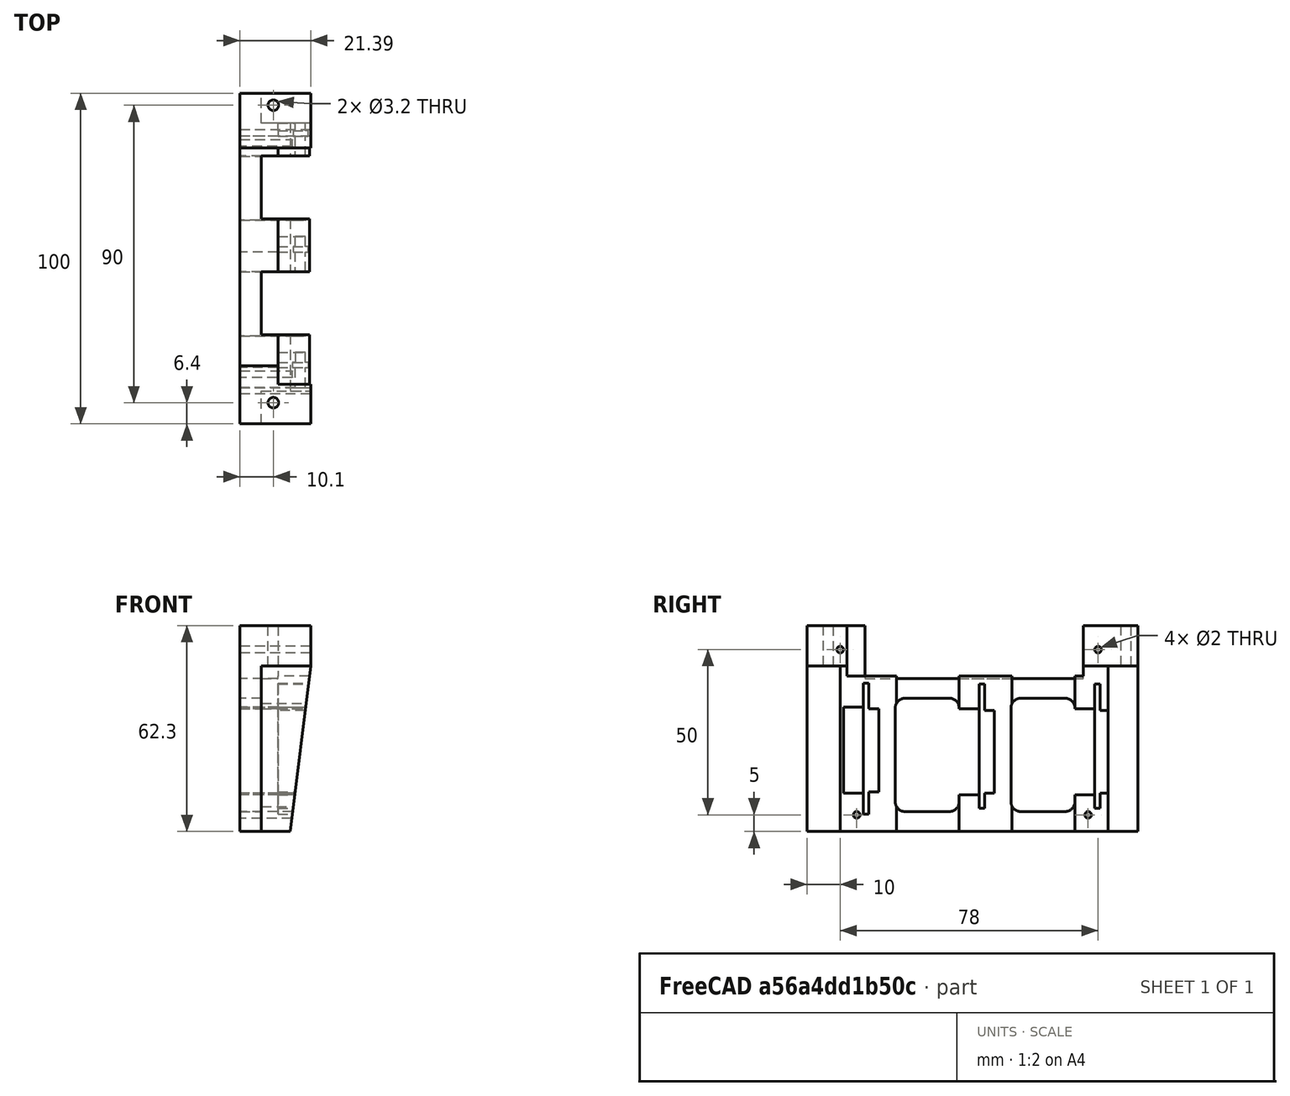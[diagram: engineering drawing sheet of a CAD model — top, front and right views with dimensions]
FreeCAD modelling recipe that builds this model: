
FCSTD DOCUMENT  (FreeCAD 1.1R40938 (Git))
Label: sborka
License: All rights reserved
LicenseURL: https://en.wikipedia.org/wiki/All_rights_reserved
objects: App::Link×10, Sketcher::SketchObject×6, PartDesign::Pocket×5, PartDesign::Pad×2, App::Point×2, Assembly::JointGroup×1, PartDesign::Body×1, Assembly::AssemblyObject×1
note: 34 computed .brp shape members not serialized (recipe doc carries the construction recipe); baked Part::Feature solids carry a one-line shape summary decoded from their .brp
EXTERNAL_REF file=lcd.FCStd obj=__97inch_LCD
EXTERNAL_REF file=ADC.FCStd obj=Board_3770
EXTERNAL_REF file=KEYPAD.FCStd obj=Body
EXTERNAL_REF file=fpga.FCStd obj=Board_4879
EXTERNAL_REF file=dac.FCStd obj=Board_2375
EXTERNAL_REF file=fpga_ext_board.FCStd obj=Board_e45
EXTERNAL_REF file=acd_dac_board.FCStd obj=Board_c5fe
EXTERNAL_REF file=power_supply.FCStd obj=Board_7c43
EXTERNAL_REF file=frontpanel.FCStd obj=Body

FEATURE [Assembly::JointGroup] Joints
FEATURE [App::Link] __97inch_LCD001  label="3_97inch_LCD001"
  LinkPlacement = pos=(582.68,421.04,26.49) rot=(0,0,-1;1.5708rad)
  LinkedObject = -> <external lcd.FCStd>#__97inch_LCD
  Placement = pos=(582.68,421.04,26.49) rot=(0,0,-1;1.5708rad)
FEATURE [App::Link] adc
  LinkPlacement = pos=(484.6,367,13) rot=(0.57735,0.57735,-0.57735;2.0944rad)
  LinkedObject = -> <external ADC.FCStd>#Board_3770
  Placement = pos=(484.6,367,13) rot=(0.57735,0.57735,-0.57735;2.0944rad)
FEATURE [App::Link] adc001
  LinkPlacement = pos=(484.6,332,13) rot=(0.57735,0.57735,-0.57735;2.0944rad)
  LinkedObject = -> <external ADC.FCStd>#Board_3770
  Placement = pos=(484.6,332,13) rot=(0.57735,0.57735,-0.57735;2.0944rad)
FEATURE [App::Link] Body  label="keypad"
  LinkPlacement = pos=(611.73,395.16,29.88) rot=(-1,0,0;1.5708rad)
  LinkedObject = -> <external KEYPAD.FCStd>#Body
  Placement = pos=(611.73,395.16,29.88) rot=(-1,0,0;1.5708rad)
FEATURE [App::Link] fpga
  LinkPlacement = pos=(542.88,295.2,49.34) rot=(0.707107,0.707107,0;3.14159rad)
  LinkedObject = -> <external fpga.FCStd>#Board_4879
  Placement = pos=(542.88,295.2,49.34) rot=(0.707107,0.707107,0;3.14159rad)
FEATURE [App::Link] dac
  LinkPlacement = pos=(481.74,297,5.5) rot=(-0.57735,-0.57735,0.57735;4.18879rad)
  LinkedObject = -> <external dac.FCStd>#Board_2375
  Placement = pos=(481.74,297,5.5) rot=(-0.57735,-0.57735,0.57735;4.18879rad)
FEATURE [App::Link] fpga_ext_board
  LinkPlacement = pos=(419,436.7,62.5) rot=(-0.707107,0.707107,0;3.14159rad)
  LinkedObject = -> <external fpga_ext_board.FCStd>#Board_e45
  Placement = pos=(419,436.7,62.5) rot=(-0.707107,0.707107,0;3.14159rad)
FEATURE [App::Link] acd_dac_board
  LinkPlacement = pos=(472,468,-70) rot=(-0.57735,0.57735,-0.57735;2.0944rad)
  LinkedObject = -> <external acd_dac_board.FCStd>#Board_c5fe
  Placement = pos=(472,468,-70) rot=(-0.57735,0.57735,-0.57735;2.0944rad)
FEATURE [Sketcher::SketchObject] Sketch
  ArcFitTolerance = 1e-06
  AttachmentSupport = -> [YZ_Plane001]
  ExternalTypes = [0]
  FullyConstrained = true
  MakeInternals = false
  MapMode = 5
  Placement = pos=(0,0,0) rot=(0.57735,0.57735,0.57735;2.0944rad)
  sketch-geometry (69):
    g0: LineSegment StartX=-33 StartY=5.25 StartZ=0 EndX=-31.36 EndY=5.25 EndZ=0
    g1: LineSegment StartX=-31.36 StartY=5.25 StartZ=0 EndX=-31.36 EndY=11.95 EndZ=0
    g2: LineSegment StartX=-31.36 StartY=44.85 StartZ=0 EndX=-33 EndY=44.85 EndZ=0
    g3: LineSegment StartX=2 StartY=7 StartZ=0 EndX=3.64 EndY=7 EndZ=0
    g4: LineSegment StartX=3.64 StartY=7 StartZ=0 EndX=3.64 EndY=11.6 EndZ=0
    g5: LineSegment StartX=3.64 StartY=44.6 StartZ=0 EndX=2 EndY=44.6 EndZ=0
    g6: LineSegment StartX=37 StartY=7 StartZ=0 EndX=38.64 EndY=7 EndZ=0
    g7: LineSegment StartX=38.64 StartY=7 StartZ=0 EndX=38.64 EndY=11.6 EndZ=0
    g8: LineSegment StartX=38.64 StartY=44.6 StartZ=0 EndX=37 EndY=44.6 EndZ=0
    g9: LineSegment StartX=-50 StartY=62.3 StartZ=0 EndX=-50 EndY=0 EndZ=0
    g10: LineSegment StartX=-50 StartY=0 StartZ=0 EndX=50 EndY=0 EndZ=0
    g11: LineSegment StartX=50 StartY=0 StartZ=0 EndX=50 EndY=62.3 EndZ=0
    g12: LineSegment StartX=-32.5 StartY=46.3 StartZ=0 EndX=33.5 EndY=46.3 EndZ=0
    g13: LineSegment StartX=-31.36 StartY=11.95 StartZ=0 EndX=-28.36 EndY=11.95 EndZ=0
    g14: LineSegment StartX=-28.36 StartY=11.95 StartZ=0 EndX=-28.36 EndY=37.15 EndZ=0
    g15: LineSegment StartX=-28.36 StartY=37.15 StartZ=0 EndX=-31.36 EndY=37.15 EndZ=0
    g16: LineSegment StartX=3.64 StartY=11.6 StartZ=0 EndX=6.64 EndY=11.6 EndZ=0
    g17: LineSegment StartX=6.64 StartY=11.6 StartZ=0 EndX=6.64 EndY=36.6 EndZ=0
    g18: LineSegment StartX=6.64 StartY=36.6 StartZ=0 EndX=3.64 EndY=36.6 EndZ=0
    g19: LineSegment StartX=38.64 StartY=11.6 StartZ=0 EndX=41.64 EndY=11.6 EndZ=0
    g20: LineSegment StartX=41.64 StartY=11.6 StartZ=0 EndX=41.64 EndY=36.6 EndZ=0
    g21: LineSegment StartX=41.64 StartY=36.6 StartZ=0 EndX=38.64 EndY=36.6 EndZ=0
    g22: LineSegment StartX=-31.36 StartY=37.15 StartZ=0 EndX=-31.36 EndY=44.85 EndZ=0
    g23: LineSegment StartX=3.64 StartY=36.6 StartZ=0 EndX=3.64 EndY=44.6 EndZ=0
    g24: LineSegment StartX=38.64 StartY=36.6 StartZ=0 EndX=38.64 EndY=44.6 EndZ=0
    g25: LineSegment StartX=-32.5 StartY=52.3 StartZ=0 EndX=33.5 EndY=52.3 EndZ=0
    g26: LineSegment StartX=-32.5 StartY=62.3 StartZ=0 EndX=-50 EndY=62.3 EndZ=0
    g27: LineSegment StartX=-32.5 StartY=62.3 StartZ=0 EndX=-32.5 EndY=52.3 EndZ=0
    g28: LineSegment StartX=-32.5 StartY=52.3 StartZ=0 EndX=-32.5 EndY=46.3 EndZ=0
    g29: LineSegment StartX=33.5 StartY=46.3 StartZ=0 EndX=33.5 EndY=52.3 EndZ=0
    g30: LineSegment StartX=33.5 StartY=52.3 StartZ=0 EndX=33.5 EndY=62.3 EndZ=0
    g31: LineSegment StartX=50 StartY=62.3 StartZ=0 EndX=33.5 EndY=62.3 EndZ=0
    g32: LineSegment StartX=-23.36 StartY=37.3 StartZ=0 EndX=-23.36 EndY=9 EndZ=0
    g33: LineSegment StartX=-20.36 StartY=6 StartZ=0 EndX=-7 EndY=6 EndZ=0
    g34: LineSegment StartX=-4 StartY=9 StartZ=0 EndX=-4 EndY=11.1 EndZ=0
    g35: LineSegment StartX=-7 StartY=40.3 StartZ=0 EndX=-20.36 EndY=40.3 EndZ=0
    g36: ArcOfCircle CenterX=-20.36 CenterY=37.3 CenterZ=0 NormalX=0 NormalY=0 NormalZ=1 AngleXU=0 Radius=3 StartAngle=1.5708 EndAngle=3.14159
    g37: ArcOfCircle CenterX=-20.36 CenterY=9 CenterZ=0 NormalX=0 NormalY=0 NormalZ=1 AngleXU=0 Radius=3 StartAngle=3.14159 EndAngle=4.71239
    g38: ArcOfCircle CenterX=-7 CenterY=9 CenterZ=0 NormalX=0 NormalY=0 NormalZ=1 AngleXU=0 Radius=3 StartAngle=4.71239 EndAngle=6.28319
    g39: ArcOfCircle CenterX=-7 CenterY=37.3 CenterZ=0 NormalX=0 NormalY=0 NormalZ=1 AngleXU=0 Radius=3 StartAngle=6.21647 EndAngle=7.85398
    g40: GeomPoint [constr] X=-23.36 Y=40.3 Z=0
    g41: GeomPoint [constr] X=-4 Y=6 Z=0
    g42: LineSegment StartX=11.64 StartY=37.3 StartZ=0 EndX=11.64 EndY=9 EndZ=0
    g43: LineSegment StartX=14.64 StartY=6 StartZ=0 EndX=28 EndY=6 EndZ=0
    g44: LineSegment StartX=31 StartY=9 StartZ=0 EndX=31 EndY=11.1 EndZ=0
    g45: LineSegment StartX=28 StartY=40.3 StartZ=0 EndX=14.64 EndY=40.3 EndZ=0
    g46: ArcOfCircle CenterX=14.64 CenterY=37.3 CenterZ=0 NormalX=0 NormalY=0 NormalZ=1 AngleXU=0 Radius=3 StartAngle=1.5708 EndAngle=3.14159
    g47: ArcOfCircle CenterX=14.64 CenterY=9 CenterZ=0 NormalX=0 NormalY=0 NormalZ=1 AngleXU=0 Radius=3 StartAngle=3.14159 EndAngle=4.71239
    g48: ArcOfCircle CenterX=28 CenterY=9 CenterZ=0 NormalX=0 NormalY=0 NormalZ=1 AngleXU=0 Radius=3 StartAngle=4.71239 EndAngle=6.28319
    g49: ArcOfCircle CenterX=28 CenterY=37.3 CenterZ=0 NormalX=0 NormalY=0 NormalZ=1 AngleXU=0 Radius=3 StartAngle=6.21647 EndAngle=7.85398
    g50: GeomPoint [constr] X=11.64 Y=40.3 Z=0
    g51: GeomPoint [constr] X=31 Y=6 Z=0
    g52: LineSegment StartX=-33 StartY=37.55 StartZ=0 EndX=-39 EndY=37.55 EndZ=0
    g53: LineSegment StartX=-39 StartY=37.55 StartZ=0 EndX=-39 EndY=11.55 EndZ=0
    g54: LineSegment StartX=-39 StartY=11.55 StartZ=0 EndX=-33 EndY=11.55 EndZ=0
    g55: LineSegment StartX=-33 StartY=11.55 StartZ=0 EndX=-33 EndY=37.55 EndZ=0
    g56: LineSegment StartX=-33 StartY=11.55 StartZ=0 EndX=-33 EndY=5.25 EndZ=0
    g57: LineSegment StartX=-33 StartY=44.85 StartZ=0 EndX=-33 EndY=37.55 EndZ=0
    g58: LineSegment StartX=-33 StartY=37.55 StartZ=0 EndX=-33 EndY=11.55 EndZ=0
    g59: LineSegment StartX=2 StartY=37.1 StartZ=0 EndX=-4.00667 EndY=37.1 EndZ=0
    g60: LineSegment StartX=2 StartY=11.1 StartZ=0 EndX=-4 EndY=11.1 EndZ=0
    g61: LineSegment StartX=37 StartY=37.1 StartZ=0 EndX=30.9933 EndY=37.1 EndZ=0
    g62: LineSegment StartX=31 StartY=11.1 StartZ=0 EndX=37 EndY=11.1 EndZ=0
    g63: LineSegment StartX=2 StartY=44.6 StartZ=0 EndX=2 EndY=37.1 EndZ=0
    g64: LineSegment StartX=2 StartY=37.1 StartZ=0 EndX=2 EndY=11.1 EndZ=0
    g65: LineSegment StartX=2 StartY=11.1 StartZ=0 EndX=2 EndY=7 EndZ=0
    g66: LineSegment StartX=37 StartY=11.1 StartZ=0 EndX=37 EndY=7 EndZ=0
    g67: LineSegment StartX=37 StartY=44.6 StartZ=0 EndX=37 EndY=37.1 EndZ=0
    g68: LineSegment StartX=37 StartY=37.1 StartZ=0 EndX=37 EndY=11.1 EndZ=0
  constraints (191):
    c: Coincident(g56,g0)
    c: Coincident(g0,g1)
    c: Coincident(g22,g2)
    c: Coincident(g2,g57)
    c: Vertical(g1)
    c: Horizontal(g0)
    c: Horizontal(g2)
    c: Distance(g57,g22) = 1.64
    c: Distance(g0,g2) = 39.6
    c: Coincident(g65,g3)
    c: Coincident(g3,g4)
    c: Coincident(g23,g5)
    c: Coincident(g5,g63)
    c: Vertical(g4)
    c: Horizontal(g3)
    c: Horizontal(g5)
    c: Distance(g63,g23) = 1.64
    c: Distance(g3,g5) = 37.6
    c: Coincident(g66,g6)
    c: Coincident(g6,g7)
    c: Coincident(g24,g8)
    c: Coincident(g8,g67)
    c: Vertical(g7)
    c: Horizontal(g6)
    c: Horizontal(g8)
    c: Distance(g67,g24) = 1.64
    c: Distance(g6,g8) = 37.6
    c: Horizontal(g23,g67)
    c: DistanceX(g63,g67) = 35
    c: DistanceX(g57,g63) = 35
    c: DistanceY(g63,g22) = 0.25
    c: Distance(g66,g-1) = 7
    c: Coincident(g9,g10)
    c: Coincident(g10,g11)
    c: Coincident(g26,g9)
    c: Vertical(g9)
    c: Vertical(g11)
    c: Horizontal(g10)
    c: PointOnObject(g10,g-1)
    c: Coincident(g28,g12)
    c: Coincident(g12,g29)
    c: Horizontal(g12)
    c: Distance(g27,g30) = 66
    c: Distance(g12,g27) = 16
    c: DistanceY(g9,g9) = 62.3
    c: DistanceX(g10,g10) = 100
    c: Coincident(g13,g14)
    c: Coincident(g14,g15)
    c: Vertical(g14)
    c: Horizontal(g13)
    c: Horizontal(g15)
    c: Distance(g15,g14) = 3
    c: Distance(g13,g15) = 25.2
    c: Distance(g56,g9) = 17
    c: DistanceY(g15,g22) = 7.7
    c: Coincident(g16,g17)
    c: Coincident(g17,g18)
    c: Vertical(g17)
    c: Horizontal(g16)
    c: Horizontal(g18)
    c: Distance(g18,g17) = 3
    c: Distance(g16,g18) = 25
    c: Coincident(g19,g20)
    c: Coincident(g20,g21)
    c: Vertical(g20)
    c: Horizontal(g19)
    c: Horizontal(g21)
    c: Distance(g21,g21) = 3
    c: DistanceY(g20,g20) = 25
    c: DistanceY(g21,g24) = 8
    c: DistanceY(g17,g23) = 8
    c: Symmetric(g9,g11,g-2)
    c: Equal(g21,g19)
    c: Equal(g13,g15)
    c: Equal(g16,g18)
    c: Coincident(g1,g13)
    c: Coincident(g4,g16)
    c: Coincident(g7,g19)
    c: Coincident(g21,g24)
    c: Coincident(g23,g18)
    c: Vertical(g24)
    c: Vertical(g23)
    c: Coincident(g22,g15)
    c: Vertical(g22)
    c: Horizontal(g25)
    c: DistanceY(g12,g25) = 6
    c: Coincident(g27,g28)
    c: Vertical(g27)
    c: Vertical(g28)
    c: Distance(g9,g27) = 17.5
    c: Coincident(g29,g30)
    c: Vertical(g29)
    c: Vertical(g30)
    c: Coincident(g27,g25)
    c: Coincident(g31,g11)
    c: Coincident(g31,g30)
    c: Horizontal(g31)
    c: Horizontal(g26)
    c: Coincident(g26,g27)
    c: Coincident(g29,g25)
    c: Tangent(g32,g36) = -1.5708
    c: Tangent(g32,g37) = -1.5708
    c: Tangent(g33,g37) = -1.5708
    c: Tangent(g33,g38) = -1.5708
    c: Tangent(g34,g38) = -1.5708
    c: Tangent(g35,g39) = -1.5708
    c: Tangent(g35,g36) = -1.5708
    c: Vertical(g32)
    c: Vertical(g34)
    c: Horizontal(g33)
    c: Horizontal(g35)
    c: Equal(g36,g37)
    c: Equal(g37,g38)
    c: Equal(g38,g39)
    c: PointOnObject(g40,g32)
    c: PointOnObject(g40,g35)
    c: PointOnObject(g41,g33)
    c: PointOnObject(g41,g34)
    c: Radius(g37) = 3
    c: Tangent(g42,g46) = -1.5708
    c: Tangent(g42,g47) = -1.5708
    c: Tangent(g43,g47) = -1.5708
    c: Tangent(g43,g48) = -1.5708
    c: Tangent(g44,g48) = -1.5708
    c: Tangent(g45,g49) = -1.5708
    c: Tangent(g45,g46) = -1.5708
    c: Vertical(g42)
    c: Vertical(g44)
    c: Horizontal(g43)
    c: Horizontal(g45)
    c: Equal(g46,g47)
    c: Equal(g47,g48)
    c: Equal(g48,g49)
    c: PointOnObject(g50,g42)
    c: PointOnObject(g50,g45)
    c: PointOnObject(g51,g43)
    c: PointOnObject(g51,g44)
    c: Radius(g47) = 3
    c: Distance(g32,g14) = 5
    c: Distance(g42,g17) = 5
    c: Distance(g35,g12) = 6
    c: Distance(g45,g12) = 6
    c: Distance(g33,g10) = 6
    c: Distance(g43,g10) = 6
    c: Coincident(g52,g53)
    c: Coincident(g53,g54)
    c: Coincident(g54,g55)
    c: Coincident(g55,g52)
    c: Horizontal(g52)
    c: Horizontal(g54)
    c: Vertical(g53)
    c: Vertical(g55)
    c: Distance(g53,g55) = 6
    c: Distance(g52,g54) = 26
    c: DistanceY(g15,g52) = 0.4
    c: Coincident(g58,g56)
    c: Vertical(g56)
    c: Coincident(g58,g54)
    c: Coincident(g57,g58)
    c: Vertical(g57)
    c: Coincident(g57,g52)
    c: Horizontal(g59)
    c: Horizontal(g60)
    c: DistanceY(g60,g4) = 0.5
    c: Coincident(g34,g60)
    c: Coincident(g39,g59)
    c: Vertical(g38,g39)
    c: DistanceX(g60,g60) = 6
    c: Horizontal(g61)
    c: Horizontal(g62)
    c: DistanceY(g62,g7) = 0.5
    c: Coincident(g44,g62)
    c: Coincident(g49,g61)
    c: Vertical(g48,g49)
    c: Distance(g18,g59) = 0.5
    c: Distance(g21,g61) = 0.5
    c: Coincident(g63,g64)
    c: Vertical(g63)
    c: PointOnObject(g60,g63)
    c: Coincident(g63,g59)
    c: Coincident(g64,g65)
    c: Vertical(g65)
    c: Coincident(g64,g60)
    c: Coincident(g68,g66)
    c: Vertical(g66)
    c: Coincident(g68,g62)
    c: Coincident(g67,g68)
    c: Vertical(g67)
    c: Vertical(g68)
    c: Distance(g44,g67) = 6
    c: Coincident(g67,g61)
FEATURE [PartDesign::Pad] Pad
  Direction = (1,0,0)
  Length = 11.5
  Length2 = 10
  Placement = pos=(0,0,0) rot=(1,1,1;2.0944rad)
  Profile = -> Sketch [Edge59,Edge60,Edge61,Edge65,Edge64,Edge63,Edge55,Edge56,Edge57,Edge58,Edge37,Edge53,Edge51,Vertex49,Edge52,Edge50,Edge49,Edge48,Edge47,Edge46,Edge45,Edge44,Edge15,Edge25,Edge26,Edge27,Edge28,Edge29,Edge30,Edge31,Edge32,Vertex30,Vertex31,Edge34,Edge33,Edge11,Edge10,Edge12,Edge9]
  ReferenceAxis = -> Sketch [N_Axis]
  Refine = true
  Reversed = true
  Suppressed = false
  Type = 0
FEATURE [PartDesign::Pad] Pad001
  BaseFeature = -> Pad
  Direction = (1,0,0)
  Length = 10
  Length2 = 10
  Placement = pos=(0,0,0) rot=(1,1,1;2.0944rad)
  Profile = -> Sketch [Edge59,Edge60,Edge61,Vertex60,Edge55,Edge56,Edge57,Vertex38,Edge40,Edge39,Edge41,Edge62,Edge43,Edge42,Edge44,Edge45,Edge46,Edge47,Edge48,Vertex34,Edge38,Edge36,Edge35,Edge54,Edge53,Vertex49,Edge52,Edge51,Edge50,Edge58,Edge49,Edge19,Edge20,Edge18,Edge17,Edge16,Edge34,Edge33,Edge32,Edge31,+22 more]
  ReferenceAxis = -> Sketch [N_Axis]
  Refine = true
  Suppressed = false
  Type = 0
FEATURE [Sketcher::SketchObject] Sketch001
  ArcFitTolerance = 1e-06
  AttachmentSupport = -> [Pad001]
  ExternalTypes = [0]
  FullyConstrained = true
  MakeInternals = false
  MapMode = 5
  Placement = pos=(0,0,-6e-16) rot=(0.707107,0.707107,0;3.14159rad)
  sketch-geometry (16):
    g0: LineSegment StartX=-23 StartY=10 StartZ=0 EndX=-23 EndY=-5 EndZ=0
    g1: LineSegment StartX=-23 StartY=-5 StartZ=0 EndX=-4 EndY=-5 EndZ=0
    g2: LineSegment StartX=-4 StartY=-5 StartZ=0 EndX=-4 EndY=10 EndZ=0
    g3: LineSegment StartX=-4 StartY=10 StartZ=0 EndX=-23 EndY=10 EndZ=0
    g4: LineSegment StartX=12 StartY=10 StartZ=0 EndX=12 EndY=-5 EndZ=0
    g5: LineSegment StartX=12 StartY=-5 StartZ=0 EndX=31 EndY=-5 EndZ=0
    g6: LineSegment StartX=31 StartY=-5 StartZ=0 EndX=31 EndY=10 EndZ=0
    g7: LineSegment StartX=31 StartY=10 StartZ=0 EndX=12 EndY=10 EndZ=0
    g8: LineSegment StartX=41 StartY=10 StartZ=0 EndX=41 EndY=-5 EndZ=0
    g9: LineSegment StartX=41 StartY=-5 StartZ=0 EndX=50 EndY=-5 EndZ=0
    g10: LineSegment StartX=50 StartY=-5 StartZ=0 EndX=50 EndY=10 EndZ=0
    g11: LineSegment StartX=50 StartY=10 StartZ=0 EndX=41 EndY=10 EndZ=0
    g12: LineSegment StartX=-40 StartY=10 StartZ=0 EndX=-50 EndY=10 EndZ=0
    g13: LineSegment StartX=-50 StartY=10 StartZ=0 EndX=-50 EndY=-5 EndZ=0
    g14: LineSegment StartX=-50 StartY=-5 StartZ=0 EndX=-40 EndY=-5 EndZ=0
    g15: LineSegment StartX=-40 StartY=-5 StartZ=0 EndX=-40 EndY=10 EndZ=0
  constraints (47):
    c: Coincident(g0,g1)
    c: Coincident(g1,g2)
    c: Coincident(g2,g3)
    c: Coincident(g3,g0)
    c: Vertical(g0)
    c: Vertical(g2)
    c: Horizontal(g1)
    c: Horizontal(g3)
    c: Coincident(g4,g5)
    c: Coincident(g5,g6)
    c: Coincident(g6,g7)
    c: Coincident(g7,g4)
    c: Vertical(g4)
    c: Vertical(g6)
    c: Horizontal(g5)
    c: Horizontal(g7)
    c: Coincident(g8,g9)
    c: Coincident(g9,g10)
    c: Coincident(g10,g11)
    c: Coincident(g11,g8)
    c: Vertical(g8)
    c: Vertical(g10)
    c: Horizontal(g9)
    c: Horizontal(g11)
    c: Coincident(g12,g13)
    c: Coincident(g13,g14)
    c: Coincident(g14,g15)
    c: Coincident(g15,g12)
    c: Horizontal(g12)
    c: Horizontal(g14)
    c: Vertical(g13)
    c: Vertical(g15)
    c: DistanceY(g13,g13) = 15
    c: Horizontal(g12,g0)
    c: Horizontal(g0,g4)
    c: Horizontal(g4,g8)
    c: Distance(g12,g12) = 10
    c: DistanceX(g13,g9) = 100
    c: Distance(g11,g11) = 9
    c: Symmetric(g13,g9,g-2)
    c: DistanceX(g12,g0) = 17
    c: DistanceX(g3,g3) = 19
    c: DistanceX(g2,g4) = 16
    c: DistanceX(g7,g7) = 19
    c: Distance(g12,g-1) = 10
    c: Horizontal(g14,g1)
    c: Horizontal(g1,g5)
FEATURE [PartDesign::Pocket] Pocket
  BaseFeature = -> Pad001
  Direction = (0,0,1)
  Length = 50
  Length2 = 5
  Placement = pos=(0,0,0) rot=(1,1,1;2.0944rad)
  Profile = -> Sketch001
  ReferenceAxis = -> Sketch001 [N_Axis]
  Suppressed = false
  Type = 0
FEATURE [Sketcher::SketchObject] Sketch002
  ArcFitTolerance = 1e-06
  AttachmentSupport = -> [Pocket]
  ExternalTypes = [0]
  FullyConstrained = true
  MakeInternals = false
  MapMode = 5
  Placement = pos=(10,0,0) rot=(0.57735,0.57735,0.57735;2.0944rad)
  sketch-geometry (4):
    g0: LineSegment StartX=-38 StartY=63 StartZ=0 EndX=-38 EndY=47 EndZ=0
    g1: LineSegment StartX=-38 StartY=47 StartZ=0 EndX=33.5 EndY=47 EndZ=0
    g2: LineSegment StartX=33.5 StartY=47 StartZ=0 EndX=33.5 EndY=63 EndZ=0
    g3: LineSegment StartX=33.5 StartY=63 StartZ=0 EndX=-38 EndY=63 EndZ=0
  constraints (12):
    c: Coincident(g0,g1)
    c: Coincident(g1,g2)
    c: Coincident(g2,g3)
    c: Coincident(g3,g0)
    c: Vertical(g0)
    c: Vertical(g2)
    c: Horizontal(g1)
    c: Horizontal(g3)
    c: Distance(g0,g0) = 16
    c: DistanceX(g1,g1) = 71.5
    c: DistanceX(g0,g-1) = 38
    c: DistanceY(g-1,g0) = 63
FEATURE [PartDesign::Pocket] Pocket001
  BaseFeature = -> Pocket
  Direction = (-1,0,0)
  Length = 10
  Length2 = 5
  Placement = pos=(0,0,0) rot=(1,1,1;2.0944rad)
  Profile = -> Sketch002
  ReferenceAxis = -> Sketch002 [N_Axis]
  Suppressed = false
  Type = 0
FEATURE [Sketcher::SketchObject] Sketch003
  ArcFitTolerance = 1e-06
  AttachmentSupport = -> [Pocket001]
  ExternalTypes = [0]
  FullyConstrained = true
  MakeInternals = false
  MapMode = 5
  Placement = pos=(-11.5,0,0) rot=(0.57735,0.57735,-0.57735;4.18879rad)
  sketch-geometry (4):
    g0: Circle CenterX=35 CenterY=-5 CenterZ=0 NormalX=0 NormalY=0 NormalZ=1 AngleXU=0 Radius=1
    g1: Circle CenterX=-35 CenterY=-5 CenterZ=0 NormalX=0 NormalY=0 NormalZ=1 AngleXU=0 Radius=1
    g2: Circle CenterX=38 CenterY=-55 CenterZ=0 NormalX=0 NormalY=0 NormalZ=1 AngleXU=0 Radius=1
    g3: Circle CenterX=-40 CenterY=-55 CenterZ=0 NormalX=0 NormalY=0 NormalZ=1 AngleXU=0 Radius=1
  constraints (12):
    c: Diameter(g0) = 2
    c: Equal(g3,g1)
    c: Equal(g0,g2)
    c: Diameter(g1) = 2
    c: Distance(g1,g-1) = 5
    c: Distance(g0,g-1) = 5
    c: Distance(g1,g-2) = 35
    c: Distance(g0,g-2) = 35
    c: Distance(g3,g-2) = 40
    c: Distance(g2,g-2) = 38
    c: Distance(g3,g-1) = 55
    c: Distance(g2,g-1) = 55
FEATURE [PartDesign::Pocket] Pocket002
  BaseFeature = -> Pocket001
  Direction = (1,0,0)
  Length = 5
  Length2 = 5
  Placement = pos=(0,0,0) rot=(1,1,1;2.0944rad)
  Profile = -> Sketch003
  ReferenceAxis = -> Sketch003 [N_Axis]
  Refine = true
  Suppressed = false
  Type = 1
FEATURE [Sketcher::SketchObject] Sketch004
  ArcFitTolerance = 1e-06
  AttachmentSupport = -> [Pocket002]
  ExternalTypes = [0]
  FullyConstrained = true
  MakeInternals = false
  MapMode = 5
  Placement = pos=(8.22e-14,2.55e-14,62.3) rot=(0,0,-1;1.5708rad)
  sketch-geometry (2):
    g0: Circle CenterX=43.6 CenterY=-1.4 CenterZ=0 NormalX=0 NormalY=0 NormalZ=1 AngleXU=0 Radius=1.6
    g1: Circle CenterX=-46.4 CenterY=-1.4 CenterZ=0 NormalX=0 NormalY=0 NormalZ=1 AngleXU=0 Radius=1.6
  constraints (6):
    c: Diameter(g0) = 3.2
    c: Diameter(g1) = 3.2
    c: DistanceY(g1,g-1) = 1.4
    c: DistanceY(g0,g-1) = 1.4
    c: DistanceX(g1,g-1) = 46.4
    c: DistanceX(g-1,g0) = 43.6
FEATURE [PartDesign::Pocket] Pocket003
  BaseFeature = -> Pocket002
  Direction = (0,0,-1)
  Length = 5
  Length2 = 5
  Placement = pos=(0,0,0) rot=(1,1,1;2.0944rad)
  Profile = -> Sketch004
  ReferenceAxis = -> Sketch004 [N_Axis]
  Refine = true
  Suppressed = false
  Type = 1
FEATURE [Sketcher::SketchObject] Sketch005
  ArcFitTolerance = 1e-06
  AttachmentSupport = -> [Pocket003]
  ExternalTypes = [0]
  FullyConstrained = false
  MakeInternals = false
  MapMode = 5
  Placement = pos=(4.15e-14,50,0) rot=(0.57735,0.57735,0.57735;4.18879rad)
  sketch-geometry (5):
    g0: LineSegment StartX=0 StartY=16.9343 StartZ=0 EndX=0 EndY=3.73792 EndZ=0
    g1: LineSegment StartX=0 StartY=3.73792 StartZ=0 EndX=50.0178 EndY=9.8851 EndZ=0
    g2: LineSegment StartX=50.0178 StartY=9.8851 StartZ=0 EndX=62.6934 EndY=9.8851 EndZ=0
    g3: LineSegment StartX=62.6934 StartY=9.8851 StartZ=0 EndX=62.6934 EndY=16.9343 EndZ=0
    g4: LineSegment StartX=62.6934 StartY=16.9343 StartZ=0 EndX=0 EndY=16.9343 EndZ=0
  constraints (9):
    c: PointOnObject(g0,g-2)
    c: PointOnObject(g0,g-2)
    c: Coincident(g1,g0)
    c: Coincident(g2,g1)
    c: Horizontal(g2)
    c: Vertical(g3)
    c: Horizontal(g4)
    c: Coincident(g0,g4)
    c: Coincident(g3,g4)
FEATURE [PartDesign::Pocket] Pocket004
  BaseFeature = -> Pocket003
  Direction = (0,-1,0)
  Length = 5
  Length2 = 5
  Placement = pos=(0,0,0) rot=(1,1,1;2.0944rad)
  Profile = -> Sketch005
  ReferenceAxis = -> Sketch005 [N_Axis]
  Refine = true
  Suppressed = false
  Type = 1
FEATURE [PartDesign::Body] Body001  label="Holder"
  AllowCompound = false
  Group = -> [Sketch,Pad,Pad001,Sketch001,Pocket,Sketch002,Pocket001,Sketch003,Pocket002,Sketch004,Pocket003,Sketch005,Pocket004]
  Origin = -> Origin001
  Placement = pos=(483.5,330,0.2) rot=(0,0,1;0rad)
  Tip = -> Pocket004
FEATURE [App::Link] power_supply
  LinkPlacement = pos=(427.54,297.43,60.5796) rot=(0.707107,-0.707107,0;3.14159rad)
  LinkedObject = -> <external power_supply.FCStd>#Board_7c43
  Placement = pos=(427.54,297.43,60.5796) rot=(0.707107,-0.707107,0;3.14159rad)
FEATURE [App::Link] front_panel001  label="front panel"
  LinkPlacement = pos=(589.68,377.5,11.4) rot=(0.57735,-0.57735,0.57735;4.18879rad)
  LinkedObject = -> <external frontpanel.FCStd>#Body
  Placement = pos=(589.68,377.5,11.4) rot=(0.57735,-0.57735,0.57735;4.18879rad)
FEATURE [Assembly::AssemblyObject] Assembly
  Group = -> [Joints,__97inch_LCD001,adc,adc001,Body,fpga,dac,fpga_ext_board,acd_dac_board,power_supply,front_panel001]
  Origin = -> Origin
  Type = Assembly
FEATURE [App::Point] Origin002  label="Початок координат"
  Role = Origin
FEATURE [App::Point] Origin003  label="Початок координат"
  Role = Origin

RESOLVED EXTERNAL PARTS (link-assembly join: the EXTERNAL_REF files above that resolve inside this repo's crawl, each included once):
---- part ADC.FCStd = doc fcstd_65c60ccaddcc ----
FCSTD DOCUMENT  (FreeCAD 1.0R39109 (Git))
Label: ADC
License: All rights reserved
LicenseURL: https://en.wikipedia.org/wiki/All_rights_reserved
objects: App::Link×34, Part::Feature×13, App::Part×4, PartDesign::CoordinateSystem×1, Sketcher::SketchObject×1
note: 16 computed .brp shape members not serialized (recipe doc carries the construction recipe); baked Part::Feature solids carry a one-line shape summary decoded from their .brp

FEATURE [PartDesign::CoordinateSystem] Local_CS_3770
  AttacherType = Attacher::AttachEngine3D
  MapMode = 2
FEATURE [Part::Feature] Pcb_3770
  Placement = pos=(-93.74,138.54,0) rot=(0,0,1;0rad)
  shape: bbox 37 x 54 x 1.6 mm, 39 faces (baked)
FEATURE [Sketcher::SketchObject] PCB_Sketch_3770
  ArcFitTolerance = 1e-06
  FullyConstrained = false
  MakeInternals = false
  sketch-geometry (4):
    g0: LineSegment StartX=-31.24 StartY=51.04 StartZ=0 EndX=5.76 EndY=51.04 EndZ=0
    g1: LineSegment StartX=5.76 StartY=51.04 StartZ=0 EndX=5.76 EndY=-2.96 EndZ=0
    g2: LineSegment StartX=5.76 StartY=-2.96 StartZ=0 EndX=-31.24 EndY=-2.96 EndZ=0
    g3: LineSegment StartX=-31.24 StartY=-2.96 StartZ=0 EndX=-31.24 EndY=51.04 EndZ=0
  constraints (4):
    c: Coincident(g2,g3)
    c: Coincident(g0,g3)
    c: Coincident(g1,g2)
    c: Coincident(g0,g1)
FEATURE [App::Part] Board_Geoms_3770
  Group = -> [Pcb_3770,PCB_Sketch_3770]
  Origin = -> Origin
FEATURE [Part::Feature] Shape  label="REF_R_1206_3216Metric_301ddd0c36ed"
  Placement = pos=(-5.34,45.84,0) rot=(0,0,1;0rad)
  shape: bbox 3.2 x 1.6 x 0.55 mm, 26 faces (baked)
FEATURE [App::Link] REF_R_1206_3216Metric_301ddd0c36ed_ln_  label="REF_REF_R_1206_3216Metric_70df84f1ae34"
  LinkPlacement = pos=(-22.84,41.94,0) rot=(0,0,1;1.5708rad)
  LinkedObject = -> Shape
  Placement = pos=(-22.84,41.94,0) rot=(0,0,1;1.5708rad)
FEATURE [App::Link] REF_R_1206_3216Metric_301ddd0c36ed_ln_001  label="REF_REF_R_1206_3216Metric_a6f854153131"
  LinkPlacement = pos=(1.16,14.24,0) rot=(0,0,1;0rad)
  LinkedObject = -> Shape
  Placement = pos=(1.16,14.24,0) rot=(0,0,1;0rad)
FEATURE [Part::Feature] Shape001  label="REF_C_1206_3216Metric_e221a3b84079"
  Placement = pos=(-9.14,29.34,0) rot=(0,0,1;0rad)
  shape: bbox 3.2 x 1.6 x 1.6 mm, 28 faces (baked)
FEATURE [App::Link] REF_R_1206_3216Metric_301ddd0c36ed_ln_002  label="REF_REF_R_1206_3216Metric_a0f92e46f677"
  LinkPlacement = pos=(-10.64,32.94,0) rot=(0,0,1;1.5708rad)
  LinkedObject = -> Shape
  Placement = pos=(-10.64,32.94,0) rot=(0,0,1;1.5708rad)
FEATURE [Part::Feature] Shape002  label="REF_CP_Elec_63x77_d1b758cef271"
  Placement = pos=(-26.34,25.34,0) rot=(0,0,1;0rad)
  shape: bbox 8.606 x 8.603 x 7.7 mm, 41 faces (baked)
FEATURE [App::Link] REF_R_1206_3216Metric_301ddd0c36ed_ln_003  label="REF_REF_R_1206_3216Metric_1b9d2568f397"
  LinkPlacement = pos=(-20.24,41.94,0) rot=(0,0,1;1.5708rad)
  LinkedObject = -> Shape
  Placement = pos=(-20.24,41.94,0) rot=(0,0,1;1.5708rad)
FEATURE [Part::Feature] Shape003  label="REF_SOIC-8-1EP_3.9x4.9mm_P1.27mm_EP2.29x3mm_4b1fed1f54c1"
  Placement = pos=(-11.94,38.14,0) rot=(0,0,1;3.14159rad)
  shape: bbox 6 x 4.9 x 1.55 mm, 152 faces (baked)
FEATURE [App::Link] REF_C_1206_3216Metric_e221a3b84079_ln_  label="REF_REF_C_1206_3216Metric_3e90dc9b15e9"
  LinkPlacement = pos=(-1.24,27.14,0) rot=(0,0,1;0rad)
  LinkedObject = -> Shape001
  Placement = pos=(-1.24,27.14,0) rot=(0,0,1;0rad)
FEATURE [App::Link] REF_C_1206_3216Metric_e221a3b84079_ln_001  label="REF_REF_C_1206_3216Metric_f21636db2d26"
  LinkPlacement = pos=(-7.14,24.54,0) rot=(0,0,1;0rad)
  LinkedObject = -> Shape001
  Placement = pos=(-7.14,24.54,0) rot=(0,0,1;0rad)
FEATURE [App::Link] REF_C_1206_3216Metric_e221a3b84079_ln_002  label="REF_REF_C_1206_3216Metric_18777c7b1951"
  LinkPlacement = pos=(-10.74,25.34,0) rot=(0,0,1;1.5708rad)
  LinkedObject = -> Shape001
  Placement = pos=(-10.74,25.34,0) rot=(0,0,1;1.5708rad)
FEATURE [App::Link] REF_R_1206_3216Metric_301ddd0c36ed_ln_004  label="REF_REF_R_1206_3216Metric_5a7a546a1d58"
  LinkPlacement = pos=(0.96,22.24,0) rot=(0,0,1;0rad)
  LinkedObject = -> Shape
  Placement = pos=(0.96,22.24,0) rot=(0,0,1;0rad)
FEATURE [App::Link] REF_R_1206_3216Metric_301ddd0c36ed_ln_005  label="REF_REF_R_1206_3216Metric_6cf90c486473"
  LinkPlacement = pos=(-18.04,8.54,0) rot=(0,0,1;1.5708rad)
  LinkedObject = -> Shape
  Placement = pos=(-18.04,8.54,0) rot=(0,0,1;1.5708rad)
FEATURE [Part::Feature] Shape004  label="REF_LED_1206_3216Metric_2fccf6a8874c"
  Placement = pos=(-21.24,30.24,0) rot=(0,0,1;1.5708rad)
  shape: bbox 1.6 x 3.2 x 1.1 mm, 50 faces (baked)
FEATURE [Part::Feature] Shape005  label="REF_PinHeader_1x02_P254mm_Vertical_da5b8ef0d3b1"
  Placement = pos=(-22.24,49.24,0) rot=(0,0,1;1.5708rad)
  shape: bbox 5.08 x 2.54 x 11.54 mm, 52 faces (baked)
FEATURE [App::Link] REF_C_1206_3216Metric_e221a3b84079_ln_003  label="REF_REF_C_1206_3216Metric_64c44e93813f"
  LinkPlacement = pos=(-16.44,19.84,0) rot=(0,0,1;1.5708rad)
  LinkedObject = -> Shape001
  Placement = pos=(-16.44,19.84,0) rot=(0,0,1;1.5708rad)
FEATURE [App::Link] REF_R_1206_3216Metric_301ddd0c36ed_ln_006  label="REF_REF_R_1206_3216Metric_3b6dfaf97a83"
  LinkPlacement = pos=(-5.34,48.74,0) rot=(0,0,1;0rad)
  LinkedObject = -> Shape
  Placement = pos=(-5.34,48.74,0) rot=(0,0,1;0rad)
FEATURE [App::Link] REF_R_1206_3216Metric_301ddd0c36ed_ln_007  label="REF_REF_R_1206_3216Metric_8c0fe4bfaf64"
  LinkPlacement = pos=(0.96,19.44,0) rot=(0,0,1;0rad)
  LinkedObject = -> Shape
  Placement = pos=(0.96,19.44,0) rot=(0,0,1;0rad)
FEATURE [App::Link] REF_C_1206_3216Metric_e221a3b84079_ln_004  label="REF_REF_C_1206_3216Metric_99c8eecee891"
  LinkPlacement = pos=(-13.14,25.34,0) rot=(0,0,1;1.5708rad)
  LinkedObject = -> Shape001
  Placement = pos=(-13.14,25.34,0) rot=(0,0,1;1.5708rad)
FEATURE [App::Link] REF_R_1206_3216Metric_301ddd0c36ed_ln_008  label="REF_REF_R_1206_3216Metric_75b0c98a4610"
  LinkPlacement = pos=(-6.34,35.04,0) rot=(0,0,1;1.5708rad)
  LinkedObject = -> Shape
  Placement = pos=(-6.34,35.04,0) rot=(0,0,1;1.5708rad)
FEATURE [App::Link] REF_C_1206_3216Metric_e221a3b84079_ln_005  label="REF_REF_C_1206_3216Metric_2542e80cc9ef"
  LinkPlacement = pos=(-4.74,29.34,0) rot=(0,0,1;0rad)
  LinkedObject = -> Shape001
  Placement = pos=(-4.74,29.34,0) rot=(0,0,1;0rad)
FEATURE [App::Link] REF_R_1206_3216Metric_301ddd0c36ed_ln_009  label="REF_REF_R_1206_3216Metric_7b8190f97f6e"
  LinkPlacement = pos=(-6.44,39.74,0) rot=(0,0,1;1.5708rad)
  LinkedObject = -> Shape
  Placement = pos=(-6.44,39.74,0) rot=(0,0,1;1.5708rad)
FEATURE [Part::Feature] Shape006  label="REF_R_Array_Concave_4x0603_6ebfddd59be7"
  Placement = pos=(-6.74,8.44,0) rot=(0,0,1;1.5708rad)
  shape: bbox 3.2 x 1.6 x 0.6 mm, 140 faces (baked)
FEATURE [App::Link] REF_C_1206_3216Metric_e221a3b84079_ln_006  label="REF_REF_C_1206_3216Metric_ddc78717e179"
  LinkPlacement = pos=(-2.54,20.84,0) rot=(0,0,1;1.5708rad)
  LinkedObject = -> Shape001
  Placement = pos=(-2.54,20.84,0) rot=(0,0,1;1.5708rad)
FEATURE [App::Link] REF_C_1206_3216Metric_e221a3b84079_ln_007  label="REF_REF_C_1206_3216Metric_0f9f458e9312"
  LinkPlacement = pos=(-26.64,39.44,0) rot=(0,0,1;0rad)
  LinkedObject = -> Shape001
  Placement = pos=(-26.64,39.44,0) rot=(0,0,1;0rad)
FEATURE [App::Link] REF_R_1206_3216Metric_301ddd0c36ed_ln_010  label="REF_REF_R_1206_3216Metric_e40d589cdbd9"
  LinkPlacement = pos=(1.06,17.04,0) rot=(0,0,1;0rad)
  LinkedObject = -> Shape
  Placement = pos=(1.06,17.04,0) rot=(0,0,1;0rad)
FEATURE [App::Link] REF_R_Array_Concave_4x0603_6ebfddd59be7_ln_  label="REF_REF_R_Array_Concave_4x0603_c1e9b6bea166"
  LinkPlacement = pos=(-10.74,8.44,0) rot=(0,0,1;1.5708rad)
  LinkedObject = -> Shape006
  Placement = pos=(-10.74,8.44,0) rot=(0,0,1;1.5708rad)
FEATURE [App::Link] REF_C_1206_3216Metric_e221a3b84079_ln_008  label="REF_REF_C_1206_3216Metric_0664d0335a5c"
  LinkPlacement = pos=(-2.54,15.14,0) rot=(0,0,1;1.5708rad)
  LinkedObject = -> Shape001
  Placement = pos=(-2.54,15.14,0) rot=(0,0,1;1.5708rad)
FEATURE [App::Link] REF_R_1206_3216Metric_301ddd0c36ed_ln_011  label="REF_REF_R_1206_3216Metric_d8d0c14688f2"
  LinkPlacement = pos=(-17.54,34.94,0) rot=(0,0,1;1.5708rad)
  LinkedObject = -> Shape
  Placement = pos=(-17.54,34.94,0) rot=(0,0,1;1.5708rad)
FEATURE [App::Link] REF_R_1206_3216Metric_301ddd0c36ed_ln_012  label="REF_REF_R_1206_3216Metric_336c34d7c97d"
  LinkPlacement = pos=(-3.84,8.34,0) rot=(0,0,1;1.5708rad)
  LinkedObject = -> Shape
  Placement = pos=(-3.84,8.34,0) rot=(0,0,1;1.5708rad)
FEATURE [Part::Feature] Shape007  label="REF_DG350-3.96-02P-12-00AH_5fb89e4e64b6"
  Placement = pos=(-23.64,20.84,0) rot=(0.57735,-0.57735,-0.57735;2.0944rad)
  shape: bbox 6.8 x 8 x 11.9 mm, 434 faces (baked)
FEATURE [App::Link] REF_C_1206_3216Metric_e221a3b84079_ln_009  label="REF_REF_C_1206_3216Metric_c52bb9b8716f"
  LinkPlacement = pos=(-3.64,39.84,0) rot=(0,0,1;1.5708rad)
  LinkedObject = -> Shape001
  Placement = pos=(-3.64,39.84,0) rot=(0,0,1;1.5708rad)
FEATURE [App::Link] REF_R_1206_3216Metric_301ddd0c36ed_ln_013  label="REF_REF_R_1206_3216Metric_975d7f625023"
  LinkPlacement = pos=(-17.14,25.54,0) rot=(0,0,1;1.5708rad)
  LinkedObject = -> Shape
  Placement = pos=(-17.14,25.54,0) rot=(0,0,1;1.5708rad)
FEATURE [App::Link] REF_C_1206_3216Metric_e221a3b84079_ln_010  label="REF_REF_C_1206_3216Metric_4ccb42aa522b"
  LinkPlacement = pos=(-7.14,26.84,0) rot=(0,0,1;0rad)
  LinkedObject = -> Shape001
  Placement = pos=(-7.14,26.84,0) rot=(0,0,1;0rad)
FEATURE [Part::Feature] Shape008  label="REF_SOT_223_e5314abddc11"
  Placement = pos=(-26.54,33.34,0) rot=(0,0,1;1.5708rad)
  shape: bbox 6.5 x 7 x 1.7 mm, 78 faces (baked)
FEATURE [Part::Feature] Shape009  label="REF_HJ-Tech-HJ-SMA175_5e94955ffa82"
  Placement = pos=(-9.14,49.04,0) rot=(0,0.707107,0.707107;3.14159rad)
  shape: bbox 8.673 x 18.44 x 9.575 mm, 56 faces (baked)
FEATURE [App::Link] REF_R_1206_3216Metric_301ddd0c36ed_ln_014  label="REF_REF_R_1206_3216Metric_01a2f680d26f"
  LinkPlacement = pos=(-21.44,34.74,0) rot=(0,0,1;1.5708rad)
  LinkedObject = -> Shape
  Placement = pos=(-21.44,34.74,0) rot=(0,0,1;1.5708rad)
FEATURE [Part::Feature] Shape010  label="REF_PinHeader_2x10_P254mm_Horizontal_88ad88291e13"
  Placement = pos=(-0.06,2.6,0) rot=(0,0,-1;1.5708rad)
  shape: bbox 25.4 x 12.9 x 8.08 mm, 484 faces (baked)
FEATURE [Part::Feature] Shape011  label="REF_LQFP_48_7x7mm_P05mm_d06fefb0920b"
  Placement = pos=(-9.84,17.34,0) rot=(0,0,1;0rad)
  shape: bbox 9 x 9 x 1.5 mm, 764 faces (baked)
FEATURE [App::Link] REF_R_1206_3216Metric_301ddd0c36ed_ln_015  label="REF_REF_R_1206_3216Metric_06fab732c749"
  LinkPlacement = pos=(-17.44,39.54,0) rot=(0,0,1;1.5708rad)
  LinkedObject = -> Shape
  Placement = pos=(-17.44,39.54,0) rot=(0,0,1;1.5708rad)
FEATURE [App::Link] REF_R_1206_3216Metric_301ddd0c36ed_ln_016  label="REF_REF_R_1206_3216Metric_0ba6753cf2ae"
  LinkPlacement = pos=(-5.44,43.24,0) rot=(0,0,1;0rad)
  LinkedObject = -> Shape
  Placement = pos=(-5.44,43.24,0) rot=(0,0,1;0rad)
FEATURE [App::Link] REF_R_1206_3216Metric_301ddd0c36ed_ln_017  label="REF_REF_R_1206_3216Metric_f8758bee8265"
  LinkPlacement = pos=(-13.04,32.94,0) rot=(0,0,1;1.5708rad)
  LinkedObject = -> Shape
  Placement = pos=(-13.04,32.94,0) rot=(0,0,1;1.5708rad)
FEATURE [App::Link] REF_R_Array_Concave_4x0603_6ebfddd59be7_ln_001  label="REF_REF_R_Array_Concave_4x0603_4768bc114470"
  LinkPlacement = pos=(-14.74,8.44,0) rot=(0,0,1;1.5708rad)
  LinkedObject = -> Shape006
  Placement = pos=(-14.74,8.44,0) rot=(0,0,1;1.5708rad)
FEATURE [App::Link] REF_C_1206_3216Metric_e221a3b84079_ln_011  label="REF_REF_C_1206_3216Metric_aac49cf074a5"
  LinkPlacement = pos=(-1.14,24.64,0) rot=(0,0,1;0rad)
  LinkedObject = -> Shape001
  Placement = pos=(-1.14,24.64,0) rot=(0,0,1;0rad)
FEATURE [App::Link] REF_C_1206_3216Metric_e221a3b84079_ln_012  label="REF_REF_C_1206_3216Metric_d76365948289"
  LinkPlacement = pos=(-3.74,35.04,0) rot=(0,0,1;1.5708rad)
  LinkedObject = -> Shape001
  Placement = pos=(-3.74,35.04,0) rot=(0,0,1;1.5708rad)
FEATURE [App::Link] REF_R_1206_3216Metric_301ddd0c36ed_ln_018  label="REF_REF_R_1206_3216Metric_e63bd7cbb3e0"
  LinkPlacement = pos=(-17.34,44.44,0) rot=(0,0,1;1.5708rad)
  LinkedObject = -> Shape
  Placement = pos=(-17.34,44.44,0) rot=(0,0,1;1.5708rad)
FEATURE [App::Part] Top_3770
  Group = -> [Shape,REF_R_1206_3216Metric_301ddd0c36ed_ln_,REF_R_1206_3216Metric_301ddd0c36ed_ln_001,Shape001,REF_R_1206_3216Metric_301ddd0c36ed_ln_002,Shape002,REF_R_1206_3216Metric_301ddd0c36ed_ln_003,Shape003,REF_C_1206_3216Metric_e221a3b84079_ln_,REF_C_1206_3216Metric_e221a3b84079_ln_001,REF_C_1206_3216Metric_e221a3b84079_ln_002,REF_R_1206_3216Metric_301ddd0c36ed_ln_004,+34 more]
  Origin = -> Origin003
FEATURE [App::Part] Step_Models_3770
  Group = -> [Top_3770]
  Origin = -> Origin002
FEATURE [App::Part] Board_3770  label="adc"
  Group = -> [Local_CS_3770,Board_Geoms_3770,Step_Models_3770]
  Origin = -> Origin001
---- part KEYPAD.FCStd = doc fcstd_31f8a50a38a9 ----
FCSTD DOCUMENT  (FreeCAD 1.1R40938 (Git))
Label: KEYPAD
License: All rights reserved
LicenseURL: https://en.wikipedia.org/wiki/All_rights_reserved
objects: Sketcher::SketchObject×1, PartDesign::Pad×1, PartDesign::Body×1, App::Point×1
note: 6 computed .brp shape members not serialized (recipe doc carries the construction recipe); baked Part::Feature solids carry a one-line shape summary decoded from their .brp

FEATURE [Sketcher::SketchObject] Sketch
  ArcFitTolerance = 1e-06
  AttachmentSupport = -> [XY_Plane]
  ExternalTypes = [0]
  FullyConstrained = true
  MakeInternals = false
  MapMode = 5
  sketch-geometry (4):
    g0: LineSegment StartX=-34.5 StartY=37.5 StartZ=0 EndX=-34.5 EndY=-37.5 EndZ=0
    g1: LineSegment StartX=-34.5 StartY=-37.5 StartZ=0 EndX=34.5 EndY=-37.5 EndZ=0
    g2: LineSegment StartX=34.5 StartY=-37.5 StartZ=0 EndX=34.5 EndY=37.5 EndZ=0
    g3: LineSegment StartX=34.5 StartY=37.5 StartZ=0 EndX=-34.5 EndY=37.5 EndZ=0
  constraints (11):
    c: Coincident(g0,g1)
    c: Coincident(g1,g2)
    c: Coincident(g2,g3)
    c: Coincident(g3,g0)
    c: Vertical(g0)
    c: Vertical(g2)
    c: Horizontal(g1)
    c: Horizontal(g3)
    c: Distance(g0,g2) = 69
    c: Distance(g1,g3) = 75
    c: Symmetric(g0,g1,g-1)
FEATURE [PartDesign::Pad] Pad
  Direction = (0,0,1)
  Length = 2
  Length2 = 10
  Profile = -> Sketch
  ReferenceAxis = -> Sketch [N_Axis]
  Refine = true
  Suppressed = false
  Type = 0
FEATURE [PartDesign::Body] Body
  AllowCompound = false
  Group = -> [Sketch,Pad]
  Origin = -> Origin
  Tip = -> Pad
FEATURE [App::Point] Origin001  label="Початок координат"
  Role = Origin
---- part acd_dac_board.FCStd = doc fcstd_6fe748700256 ----
FCSTD DOCUMENT  (FreeCAD 1.0R39109 (Git))
Label: acd_dac_board
License: All rights reserved
LicenseURL: https://en.wikipedia.org/wiki/All_rights_reserved
objects: App::Part×6, App::Link×5, Part::Feature×4, PartDesign::CoordinateSystem×1, Sketcher::SketchObject×1
note: 7 computed .brp shape members not serialized (recipe doc carries the construction recipe); baked Part::Feature solids carry a one-line shape summary decoded from their .brp

FEATURE [PartDesign::CoordinateSystem] Local_CS_c5fe
  AttacherType = Attacher::AttachEngine3D
  MapMode = 2
FEATURE [Part::Feature] Pcb_c5fe
  shape: bbox 90 x 60 x 1.6 mm, 120 faces (baked)
FEATURE [Sketcher::SketchObject] PCB_Sketch_c5fe
  ArcFitTolerance = 1e-06
  FullyConstrained = false
  MakeInternals = false
  sketch-geometry (4):
    g0: LineSegment StartX=93.9 StartY=-71.9 StartZ=0 EndX=183.9 EndY=-71.9 EndZ=0
    g1: LineSegment StartX=183.9 StartY=-71.9 StartZ=0 EndX=183.9 EndY=-131.9 EndZ=0
    g2: LineSegment StartX=183.9 StartY=-131.9 StartZ=0 EndX=93.9 EndY=-131.9 EndZ=0
    g3: LineSegment StartX=93.9 StartY=-131.9 StartZ=0 EndX=93.9 EndY=-71.9 EndZ=0
  constraints (4):
    c: Coincident(g2,g3)
    c: Coincident(g0,g3)
    c: Coincident(g1,g2)
    c: Coincident(g0,g1)
FEATURE [App::Part] Board_Geoms_c5fe
  Group = -> [Pcb_c5fe,PCB_Sketch_c5fe]
  Origin = -> Origin
FEATURE [Part::Feature] Shape  label="J4_PinHeader_2x25_P254mm_Horizontal_27a54bd5aef3"
  Placement = pos=(168.5,-117.06,0) rot=(0,0,-1;1.5708rad)
  shape: bbox 63.5 x 12.9 x 8.08 mm, 1204 faces (baked)
FEATURE [Part::Feature] Shape001  label="J3_PinSocket_2x10_P2.54mm_Vertical_5a6bbbb15814"
  Placement = pos=(174.8,-83.06,0) rot=(0,0,1;0rad)
  shape: bbox 5.08 x 25.4 x 11.6 mm, 530 faces (baked)
FEATURE [App::Link] J3_PinSocket_2x10_P2_54mm_Vertical_5a6bbbb15814_ln_  label="J1_PinSocket_2x10_P2.54mm_Vertical_580dcfef748e"
  LinkPlacement = pos=(104.8,-83.06,0) rot=(0,0,1;0rad)
  LinkedObject = -> Shape001
  Placement = pos=(104.8,-83.06,0) rot=(0,0,1;0rad)
FEATURE [App::Link] J3_PinSocket_2x10_P2_54mm_Vertical_5a6bbbb15814_ln_001  label="J2_PinSocket_2x10_P2.54mm_Vertical_61ef51b03cdf"
  LinkPlacement = pos=(139.8,-83.06,0) rot=(0,0,1;0rad)
  LinkedObject = -> Shape001
  Placement = pos=(139.8,-83.06,0) rot=(0,0,1;0rad)
FEATURE [App::Part] Top_c5fe
  Group = -> [Shape,Shape001,J3_PinSocket_2x10_P2_54mm_Vertical_5a6bbbb15814_ln_,J3_PinSocket_2x10_P2_54mm_Vertical_5a6bbbb15814_ln_001]
  Origin = -> Origin003
FEATURE [App::Part] Step_Models_c5fe
  Group = -> [Top_c5fe]
  Origin = -> Origin002
FEATURE [Part::Feature] Shape002  label="REF_2.5 mmx7-Screw_fc498af58895"
  Placement = pos=(173,-75.1,-1.6) rot=(0,1,0;3.14159rad)
  shape: bbox 5 x 5 x 8.693 mm, 8 faces (baked)
FEATURE [App::Link] REF_2_5_mmx7_Screw_fc498af58895_ln_  label="REF_REF_2.5 mmx7-Screw_7bb2b2d65ce1"
  LinkPlacement = pos=(178,-125.1,-1.6) rot=(0,1,0;3.14159rad)
  LinkedObject = -> Shape002
  Placement = pos=(178,-125.1,-1.6) rot=(0,1,0;3.14159rad)
FEATURE [App::Link] REF_2_5_mmx7_Screw_fc498af58895_ln_001  label="REF_REF_2.5 mmx7-Screw_5b3bb718906a"
  LinkPlacement = pos=(99.9,-125.1,-1.6) rot=(0,1,0;3.14159rad)
  LinkedObject = -> Shape002
  Placement = pos=(99.9,-125.1,-1.6) rot=(0,1,0;3.14159rad)
FEATURE [App::Link] REF_2_5_mmx7_Screw_fc498af58895_ln_002  label="REF_REF_2.5 mmx7-Screw_1ec84486e3c5"
  LinkPlacement = pos=(103,-75.1,-1.6) rot=(0,1,0;3.14159rad)
  LinkedObject = -> Shape002
  Placement = pos=(103,-75.1,-1.6) rot=(0,1,0;3.14159rad)
FEATURE [App::Part] BotV_c5fe
  Group = -> [Shape002,REF_2_5_mmx7_Screw_fc498af58895_ln_,REF_2_5_mmx7_Screw_fc498af58895_ln_001,REF_2_5_mmx7_Screw_fc498af58895_ln_002]
  Origin = -> Origin007
FEATURE [App::Part] Step_Virtual_Models_c5fe
  Group = -> [BotV_c5fe]
  Origin = -> Origin005
FEATURE [App::Part] Board_c5fe  label="acd_dac_board"
  Group = -> [Local_CS_c5fe,Board_Geoms_c5fe,Step_Models_c5fe,Step_Virtual_Models_c5fe]
  Origin = -> Origin001
---- part dac.FCStd = doc fcstd_b249aee94d24 ----
FCSTD DOCUMENT  (FreeCAD 1.0R39109 (Git))
Label: dac
License: All rights reserved
LicenseURL: https://en.wikipedia.org/wiki/All_rights_reserved
objects: App::Link×47, Part::Feature×22, App::Part×10, PartDesign::CoordinateSystem×1, Sketcher::SketchObject×1
note: 25 computed .brp shape members not serialized (recipe doc carries the construction recipe); baked Part::Feature solids carry a one-line shape summary decoded from their .brp

FEATURE [PartDesign::CoordinateSystem] Local_CS_2375
  AttacherType = Attacher::AttachEngine3D
  MapMode = 2
FEATURE [Part::Feature] Pcb_2375
  Placement = pos=(-126.3,128.5,0) rot=(0,0,1;0rad)
  shape: bbox 39 x 56 x 1.6 mm, 70 faces (baked)
FEATURE [Sketcher::SketchObject] PCB_Sketch_2375
  ArcFitTolerance = 1e-06
  FullyConstrained = false
  MakeInternals = false
  sketch-geometry (4):
    g0: LineSegment StartX=-39 StartY=56 StartZ=0 EndX=0 EndY=56 EndZ=0
    g1: LineSegment StartX=0 StartY=56 StartZ=0 EndX=0 EndY=0 EndZ=0
    g2: LineSegment StartX=0 StartY=0 StartZ=0 EndX=-39 EndY=0 EndZ=0
    g3: LineSegment StartX=-39 StartY=0 StartZ=0 EndX=-39 EndY=56 EndZ=0
  constraints (4):
    c: Coincident(g2,g3)
    c: Coincident(g0,g3)
    c: Coincident(g1,g2)
    c: Coincident(g0,g1)
FEATURE [App::Part] Board_Geoms_2375
  Group = -> [Pcb_2375,PCB_Sketch_2375]
  Origin = -> Origin
FEATURE [Part::Feature] Shape  label="REF_TSSOP_28_44x97mm_P065mm_c3a42edb85d4"
  Placement = pos=(-16,18.3,0) rot=(0,0,1;1.5708rad)
  shape: bbox 9.7 x 6.4 x 1.1 mm, 456 faces (baked)
FEATURE [Part::Feature] Shape001  label="REF_R_1206_3216Metric_dea5eb461704"
  Placement = pos=(-13.3,41.1,0) rot=(0,0,1;1.5708rad)
  shape: bbox 1.6 x 3.2 x 0.55 mm, 26 faces (baked)
FEATURE [Part::Feature] Shape002  label="REF_L_1206_3216Metric_923911bd139e"
  Placement = pos=(-23.4,26.9,0) rot=(0,0,1;1.5708rad)
  shape: bbox 1.6 x 3.2 x 1.6 mm, 28 faces (baked)
FEATURE [Part::Feature] Shape003  label="REF_R_Array_Convex_4x0603_e66b4cefd16a"
  Placement = pos=(-18.3333,10.6,0) rot=(0,0,1;1.5708rad)
  shape: bbox 3.2 x 1.6 x 0.5 mm, 206 faces (baked)
FEATURE [Part::Feature] Shape004  label="REF_C_1812_4532Metric_fd35fdb9ec24"
  Placement = pos=(-34.9,37.2,0) rot=(0,0,1;0rad)
  shape: bbox 4.5 x 3.2 x 2.5 mm, 28 faces (baked)
FEATURE [Part::Feature] Shape005  label="REF_CP_Elec_63x77_0427d7c4acbc"
  Placement = pos=(-27.5,34.4,0) rot=(0,0,1;0rad)
  shape: bbox 8.606 x 8.603 x 7.7 mm, 41 faces (baked)
FEATURE [Part::Feature] Shape006  label="REF_D_SMA_bc62c40d3f1a"
  Placement = pos=(-35,30.6,0) rot=(0,0,1;0rad)
  shape: bbox 5 x 2.7 x 2.22 mm, 41 faces (baked)
FEATURE [App::Link] REF_R_Array_Convex_4x0603_e66b4cefd16a_ln_  label="REF_REF_R_Array_Convex_4x0603_60d2f3ed0a64"
  LinkPlacement = pos=(-14.1667,10.6,0) rot=(0,0,1;1.5708rad)
  LinkedObject = -> Shape003
  Placement = pos=(-14.1667,10.6,0) rot=(0,0,1;1.5708rad)
FEATURE [App::Link] REF_L_1206_3216Metric_923911bd139e_ln_  label="REF_REF_L_1206_3216Metric_92d995cbed52"
  LinkPlacement = pos=(-25.7,26.9,0) rot=(0,0,1;1.5708rad)
  LinkedObject = -> Shape002
  Placement = pos=(-25.7,26.9,0) rot=(0,0,1;1.5708rad)
FEATURE [Part::Feature] Shape007  label="REF_C_1206_3216Metric_ecc4e7f1350d"
  Placement = pos=(-25,21.6,0) rot=(0,0,1;3.14159rad)
  shape: bbox 3.2 x 1.6 x 1.6 mm, 28 faces (baked)
FEATURE [App::Link] REF_C_1206_3216Metric_ecc4e7f1350d_ln_  label="REF_REF_C_1206_3216Metric_d5ebf2718203"
  LinkPlacement = pos=(-9.4,26.9,0) rot=(0,0,1;1.5708rad)
  LinkedObject = -> Shape007
  Placement = pos=(-9.4,26.9,0) rot=(0,0,1;1.5708rad)
FEATURE [Part::Feature] Shape008  label="REF_PinHeader_2x10_P254mm_Horizontal_c3ac748f6938"
  Placement = pos=(-7.5,5.5,0) rot=(0,0,-1;1.5708rad)
  shape: bbox 25.4 x 12.9 x 8.08 mm, 484 faces (baked)
FEATURE [Part::Feature] Shape009  label="REF_PinHeader_1x02_P254mm_Vertical_c2c35adffc7d"
  Placement = pos=(-6.1,18,0) rot=(0,0,1;0rad)
  shape: bbox 2.54 x 5.08 x 11.54 mm, 52 faces (baked)
FEATURE [Part::Feature] Part__Feature  label="adbeea57-9c39-11ed-93f0-dde97e994e83_part"
  shape: bbox 2.5 x 4.5 x 1.5 mm, 12 faces (baked)
FEATURE [App::Part] adbeea57_9c39_11ed_93f0_dde97e994e83  label="adbeea57-9c39-11ed-93f0-dde97e994e83"
  Group = -> [Part__Feature]
  Origin = -> Origin008
FEATURE [Part::Feature] Part__Feature001  label="adbeea58-9c39-11ed-93f0-dde97e994e83_part"
  shape: bbox 2.5 x 1.6 x 0.4 mm, 12 faces (baked)
FEATURE [App::Part] adbeea58_9c39_11ed_93f0_dde97e994e83  label="adbeea58-9c39-11ed-93f0-dde97e994e83"
  Group = -> [Part__Feature001]
  Origin = -> Origin009
FEATURE [Part::Feature] Part__Feature002  label="adbeea59-9c39-11ed-93f0-dde97e994e83_part"
  shape: bbox 1.5 x 0.4 x 0.4 mm, 6 faces (baked)
FEATURE [Part::Feature] Part__Feature003  label="adbeea59-9c39-11ed-93f0-dde97e994e83_part001"
  shape: bbox 1.5 x 0.4 x 0.4 mm, 6 faces (baked)
FEATURE [Part::Feature] Part__Feature004  label="adbeea59-9c39-11ed-93f0-dde97e994e83_part002"
  shape: bbox 1.5 x 0.4 x 0.4 mm, 6 faces (baked)
FEATURE [App::Part] adbeea59_9c39_11ed_93f0_dde97e994e83_part  label="adbeea59-9c39-11ed-93f0-dde97e994e83_part003"
  Group = -> [Part__Feature002,Part__Feature003,Part__Feature004]
  Origin = -> Origin010
FEATURE [App::Part] adbeea59_9c39_11ed_93f0_dde97e994e83  label="adbeea59-9c39-11ed-93f0-dde97e994e83"
  Group = -> [adbeea59_9c39_11ed_93f0_dde97e994e83_part]
  Origin = -> Origin011
FEATURE [App::Part] adbeea56_9c39_11ed_93f0_dde97e994e83  label="adbeea56-9c39-11ed-93f0-dde97e994e83"
  Group = -> [adbeea57_9c39_11ed_93f0_dde97e994e83,adbeea58_9c39_11ed_93f0_dde97e994e83,adbeea59_9c39_11ed_93f0_dde97e994e83]
  Origin = -> Origin012
FEATURE [App::Part] CQ_assembly  label="REF_CQ assembly_e2316aff6ff6"
  Group = -> [adbeea56_9c39_11ed_93f0_dde97e994e83]
  Origin = -> Origin013
  Placement = pos=(-25.6,18.4,0) rot=(0,0,1;3.14159rad)
FEATURE [App::Link] REF_PinHeader_1x02_P254mm_Vertical_c2c35adffc7d_ln_  label="REF_REF_PinHeader_1x02_P254mm_Vertical_8d209ac5472d"
  LinkPlacement = pos=(-28,51.7,0) rot=(0,0,1;1.5708rad)
  LinkedObject = -> Shape009
  Placement = pos=(-28,51.7,0) rot=(0,0,1;1.5708rad)
FEATURE [App::Link] REF_R_1206_3216Metric_dea5eb461704_ln_  label="REF_REF_R_1206_3216Metric_28bc4882b059"
  LinkPlacement = pos=(-15.7,41.2,0) rot=(0,0,1;1.5708rad)
  LinkedObject = -> Shape001
  Placement = pos=(-15.7,41.2,0) rot=(0,0,1;1.5708rad)
FEATURE [App::Link] REF_C_1206_3216Metric_ecc4e7f1350d_ln_001  label="REF_REF_C_1206_3216Metric_9cc814834820"
  LinkPlacement = pos=(-18.7,26.9,0) rot=(0,0,1;1.5708rad)
  LinkedObject = -> Shape007
  Placement = pos=(-18.7,26.9,0) rot=(0,0,1;1.5708rad)
FEATURE [App::Link] REF_C_1206_3216Metric_ecc4e7f1350d_ln_002  label="REF_REF_C_1206_3216Metric_140ac1610760"
  LinkPlacement = pos=(-4.6,41.2,0) rot=(0,0,1;1.5708rad)
  LinkedObject = -> Shape007
  Placement = pos=(-4.6,41.2,0) rot=(0,0,1;1.5708rad)
FEATURE [Part::Feature] Shape010  label="REF_L_Cenker_CKCS4030_d8273a953477"
  Placement = pos=(-32,26,0) rot=(0,0,1;1.5708rad)
  shape: bbox 4 x 4.02 x 3 mm, 28 faces (baked)
FEATURE [App::Link] REF_C_1206_3216Metric_ecc4e7f1350d_ln_003  label="REF_REF_C_1206_3216Metric_1bdc9c04c953"
  LinkPlacement = pos=(-28.1,26.9,0) rot=(0,0,1;1.5708rad)
  LinkedObject = -> Shape007
  Placement = pos=(-28.1,26.9,0) rot=(0,0,1;1.5708rad)
FEATURE [App::Link] REF_C_1206_3216Metric_ecc4e7f1350d_ln_004  label="REF_REF_C_1206_3216Metric_cb06a00eb6bb"
  LinkPlacement = pos=(-14.1,26.9,0) rot=(0,0,1;1.5708rad)
  LinkedObject = -> Shape007
  Placement = pos=(-14.1,26.9,0) rot=(0,0,1;1.5708rad)
FEATURE [App::Link] REF_C_1206_3216Metric_ecc4e7f1350d_ln_005  label="REF_REF_C_1206_3216Metric_edc837841e0f"
  LinkPlacement = pos=(-14.5,36,0) rot=(0,0,1;1.5708rad)
  LinkedObject = -> Shape007
  Placement = pos=(-14.5,36,0) rot=(0,0,1;1.5708rad)
FEATURE [App::Link] REF_C_1206_3216Metric_ecc4e7f1350d_ln_006  label="REF_REF_C_1206_3216Metric_872d7316da85"
  LinkPlacement = pos=(-11.8,36,0) rot=(0,0,1;1.5708rad)
  LinkedObject = -> Shape007
  Placement = pos=(-11.8,36,0) rot=(0,0,1;1.5708rad)
FEATURE [App::Link] REF_C_1206_3216Metric_ecc4e7f1350d_ln_007  label="REF_REF_C_1206_3216Metric_fa080edd5de2"
  LinkPlacement = pos=(-34.7,33.7,0) rot=(0,0,1;3.14159rad)
  LinkedObject = -> Shape007
  Placement = pos=(-34.7,33.7,0) rot=(0,0,1;3.14159rad)
FEATURE [App::Link] REF_R_1206_3216Metric_dea5eb461704_ln_001  label="REF_REF_R_1206_3216Metric_daaedf7f6707"
  LinkPlacement = pos=(-7,26.9,0) rot=(0,0,1;1.5708rad)
  LinkedObject = -> Shape001
  Placement = pos=(-7,26.9,0) rot=(0,0,1;1.5708rad)
FEATURE [App::Link] REF_R_1206_3216Metric_dea5eb461704_ln_002  label="REF_REF_R_1206_3216Metric_e0c93ad1cb2a"
  LinkPlacement = pos=(-15.7,45.2,0) rot=(0,0,1;1.5708rad)
  LinkedObject = -> Shape001
  Placement = pos=(-15.7,45.2,0) rot=(0,0,1;1.5708rad)
FEATURE [Part::Feature] Shape011  label="REF_L_1210_3225Metric_5d334701bb60"
  Placement = pos=(-12.8,32.2,0) rot=(0,0,1;0rad)
  shape: bbox 3.2 x 2.5 x 2.5 mm, 28 faces (baked)
FEATURE [App::Link] REF_R_Array_Convex_4x0603_e66b4cefd16a_ln_001  label="REF_REF_R_Array_Convex_4x0603_f7815705a583"
  LinkPlacement = pos=(-22.5,10.6,0) rot=(0,0,1;1.5708rad)
  LinkedObject = -> Shape003
  Placement = pos=(-22.5,10.6,0) rot=(0,0,1;1.5708rad)
FEATURE [App::Link] REF_C_1206_3216Metric_ecc4e7f1350d_ln_008  label="REF_REF_C_1206_3216Metric_7a416d868406"
  LinkPlacement = pos=(-26.5,48.5,0) rot=(0,0,1;3.14159rad)
  LinkedObject = -> Shape007
  Placement = pos=(-26.5,48.5,0) rot=(0,0,1;3.14159rad)
FEATURE [App::Link] REF_L_1210_3225Metric_5d334701bb60_ln_  label="REF_REF_L_1210_3225Metric_272e2f4baf41"
  LinkPlacement = pos=(-17,32.2,0) rot=(0,0,1;0rad)
  LinkedObject = -> Shape011
  Placement = pos=(-17,32.2,0) rot=(0,0,1;0rad)
FEATURE [App::Link] REF_R_1206_3216Metric_dea5eb461704_ln_003  label="REF_REF_R_1206_3216Metric_4bb3a19c4e52"
  LinkPlacement = pos=(-22.1,36,0) rot=(0,0,1;1.5708rad)
  LinkedObject = -> Shape001
  Placement = pos=(-22.1,36,0) rot=(0,0,1;1.5708rad)
FEATURE [App::Link] REF_PinHeader_1x02_P254mm_Vertical_c2c35adffc7d_ln_001  label="REF_REF_PinHeader_1x02_P254mm_Vertical_c0119e070db1"
  LinkPlacement = pos=(-2.6,18,0) rot=(0,0,1;0rad)
  LinkedObject = -> Shape009
  Placement = pos=(-2.6,18,0) rot=(0,0,1;0rad)
FEATURE [Part::Feature] Shape012  label="REF_SOIC-8-1EP_3.9x4.9mm_P1.27mm_EP2.29x3mm_2a411558dc4c"
  Placement = pos=(-34.95,42.77,0) rot=(0,0,1;1.5708rad)
  shape: bbox 4.9 x 6 x 1.55 mm, 152 faces (baked)
FEATURE [App::Link] REF_L_1206_3216Metric_923911bd139e_ln_001  label="REF_REF_L_1206_3216Metric_39378e988feb"
  LinkPlacement = pos=(-21.2,26.9,0) rot=(0,0,1;1.5708rad)
  LinkedObject = -> Shape002
  Placement = pos=(-21.2,26.9,0) rot=(0,0,1;1.5708rad)
FEATURE [App::Link] REF_C_1812_4532Metric_fd35fdb9ec24_ln_  label="REF_REF_C_1812_4532Metric_d066acd0d603"
  LinkPlacement = pos=(-36.5,25.9,0) rot=(0,0,1;1.5708rad)
  LinkedObject = -> Shape004
  Placement = pos=(-36.5,25.9,0) rot=(0,0,1;1.5708rad)
FEATURE [App::Link] REF_L_1210_3225Metric_5d334701bb60_ln_001  label="REF_REF_L_1210_3225Metric_7fdfb9fc9615"
  LinkPlacement = pos=(-21.3,32.2,0) rot=(0,0,1;0rad)
  LinkedObject = -> Shape011
  Placement = pos=(-21.3,32.2,0) rot=(0,0,1;0rad)
FEATURE [App::Link] REF_R_1206_3216Metric_dea5eb461704_ln_004  label="REF_REF_R_1206_3216Metric_3d4d2a619084"
  LinkPlacement = pos=(-19,49.3,0) rot=(0,0,1;1.5708rad)
  LinkedObject = -> Shape001
  Placement = pos=(-19,49.3,0) rot=(0,0,1;1.5708rad)
FEATURE [App::Link] REF_C_1206_3216Metric_ecc4e7f1350d_ln_009  label="REF_REF_C_1206_3216Metric_46c0f67f32fe"
  LinkPlacement = pos=(-14.3,48.5,0) rot=(0,0,1;3.14159rad)
  LinkedObject = -> Shape007
  Placement = pos=(-14.3,48.5,0) rot=(0,0,1;3.14159rad)
FEATURE [App::Link] REF_R_1206_3216Metric_dea5eb461704_ln_005  label="REF_REF_R_1206_3216Metric_589fc75ea92f"
  LinkPlacement = pos=(-4.7,31.3,0) rot=(0,0,1;1.5708rad)
  LinkedObject = -> Shape001
  Placement = pos=(-4.7,31.3,0) rot=(0,0,1;1.5708rad)
FEATURE [App::Link] REF_SOIC_8_1EP_3_9x4_9mm_P1_27mm_EP2_29x3mm_2a411558dc4c_ln_  label="REF_REF_SOIC-8-1EP_3.9x4.9mm_P1.27mm_EP2.29x3mm_327c7d781933"
  LinkPlacement = pos=(-8.65,42.77,0) rot=(0,0,1;1.5708rad)
  LinkedObject = -> Shape012
  Placement = pos=(-8.65,42.77,0) rot=(0,0,1;1.5708rad)
FEATURE [App::Link] REF_R_1206_3216Metric_dea5eb461704_ln_006  label="REF_REF_R_1206_3216Metric_e1e13a756e31"
  LinkPlacement = pos=(-9.5,31.4,0) rot=(0,0,1;1.5708rad)
  LinkedObject = -> Shape001
  Placement = pos=(-9.5,31.4,0) rot=(0,0,1;1.5708rad)
FEATURE [App::Link] REF_C_1206_3216Metric_ecc4e7f1350d_ln_010  label="REF_REF_C_1206_3216Metric_d8d913f8484a"
  LinkPlacement = pos=(-11.8,26.9,0) rot=(0,0,1;1.5708rad)
  LinkedObject = -> Shape007
  Placement = pos=(-11.8,26.9,0) rot=(0,0,1;1.5708rad)
FEATURE [App::Link] REF_R_1206_3216Metric_dea5eb461704_ln_007  label="REF_REF_R_1206_3216Metric_857049673542"
  LinkPlacement = pos=(-4.6,36,0) rot=(0,0,1;1.5708rad)
  LinkedObject = -> Shape001
  Placement = pos=(-4.6,36,0) rot=(0,0,1;1.5708rad)
FEATURE [Part::Feature] Shape013  label="REF_LED_1206_3216Metric_d22cfbdbfb4d"
  Placement = pos=(-28.5,11.3,0) rot=(0,0,1;1.5708rad)
  shape: bbox 1.6 x 3.2 x 1.1 mm, 50 faces (baked)
FEATURE [App::Link] REF_C_1206_3216Metric_ecc4e7f1350d_ln_011  label="REF_REF_C_1206_3216Metric_7f81c6af838c"
  LinkPlacement = pos=(-19.6,36,0) rot=(0,0,1;1.5708rad)
  LinkedObject = -> Shape007
  Placement = pos=(-19.6,36,0) rot=(0,0,1;1.5708rad)
FEATURE [App::Link] REF_C_1206_3216Metric_ecc4e7f1350d_ln_012  label="REF_REF_C_1206_3216Metric_c4aa7e021370"
  LinkPlacement = pos=(-13.4,45.2,0) rot=(0,0,1;1.5708rad)
  LinkedObject = -> Shape007
  Placement = pos=(-13.4,45.2,0) rot=(0,0,1;1.5708rad)
FEATURE [App::Link] REF_C_1206_3216Metric_ecc4e7f1350d_ln_013  label="REF_REF_C_1206_3216Metric_57fe54d1a34d"
  LinkPlacement = pos=(-24.2,45.1,0) rot=(0,0,1;1.5708rad)
  LinkedObject = -> Shape007
  Placement = pos=(-24.2,45.1,0) rot=(0,0,1;1.5708rad)
FEATURE [Part::Feature] Shape014  label="REF_SMA_Samtec_SMA-J-P-H-ST-EM1_EdgeMount_10ab1944b6c5"
  Placement = pos=(-19.2,54.4375,0) rot=(0,0,1;1.5708rad)
  shape: bbox 6.633 x 13.33 x 6.523 mm, 69 faces (baked)
FEATURE [App::Link] REF_R_1206_3216Metric_dea5eb461704_ln_008  label="REF_REF_R_1206_3216Metric_5fd7c2efb940"
  LinkPlacement = pos=(-7,31.3,0) rot=(0,0,1;1.5708rad)
  LinkedObject = -> Shape001
  Placement = pos=(-7,31.3,0) rot=(0,0,1;1.5708rad)
FEATURE [App::Link] REF_R_1206_3216Metric_dea5eb461704_ln_009  label="REF_REF_R_1206_3216Metric_8f214b9c0e7f"
  LinkPlacement = pos=(-9.5,36,0) rot=(0,0,1;1.5708rad)
  LinkedObject = -> Shape001
  Placement = pos=(-9.5,36,0) rot=(0,0,1;1.5708rad)
FEATURE [App::Link] REF_C_1206_3216Metric_ecc4e7f1350d_ln_014  label="REF_REF_C_1206_3216Metric_6b1bf2e510a7"
  LinkPlacement = pos=(-22.4,48.5,0) rot=(0,0,1;3.14159rad)
  LinkedObject = -> Shape007
  Placement = pos=(-22.4,48.5,0) rot=(0,0,1;3.14159rad)
FEATURE [App::Link] REF_R_1206_3216Metric_dea5eb461704_ln_010  label="REF_REF_R_1206_3216Metric_47425226c818"
  LinkPlacement = pos=(-16.3,26.9,0) rot=(0,0,1;1.5708rad)
  LinkedObject = -> Shape001
  Placement = pos=(-16.3,26.9,0) rot=(0,0,1;1.5708rad)
FEATURE [App::Link] REF_R_1206_3216Metric_dea5eb461704_ln_011  label="REF_REF_R_1206_3216Metric_96f9e62eec0e"
  LinkPlacement = pos=(-7.1,36,0) rot=(0,0,1;1.5708rad)
  LinkedObject = -> Shape001
  Placement = pos=(-7.1,36,0) rot=(0,0,1;1.5708rad)
FEATURE [App::Link] REF_R_1206_3216Metric_dea5eb461704_ln_012  label="REF_REF_R_1206_3216Metric_56ab30c5af69"
  LinkPlacement = pos=(-25.8,11,0) rot=(0,0,1;1.5708rad)
  LinkedObject = -> Shape001
  Placement = pos=(-25.8,11,0) rot=(0,0,1;1.5708rad)
FEATURE [App::Link] REF_R_Array_Convex_4x0603_e66b4cefd16a_ln_002  label="REF_REF_R_Array_Convex_4x0603_f290d0503860"
  LinkPlacement = pos=(-10,10.6,0) rot=(0,0,1;1.5708rad)
  LinkedObject = -> Shape003
  Placement = pos=(-10,10.6,0) rot=(0,0,1;1.5708rad)
FEATURE [App::Link] REF_C_1206_3216Metric_ecc4e7f1350d_ln_015  label="REF_REF_C_1206_3216Metric_dc8951aa932c"
  LinkPlacement = pos=(-24.8,14.8,0) rot=(0,0,1;3.14159rad)
  LinkedObject = -> Shape007
  Placement = pos=(-24.8,14.8,0) rot=(0,0,1;3.14159rad)
FEATURE [Part::Feature] Shape015  label="REF_DG350-3.96-02P-12-00AH_d845d113af01"
  Placement = pos=(-31.7,20.8,0) rot=(0.57735,-0.57735,-0.57735;2.0944rad)
  shape: bbox 6.8 x 8 x 11.9 mm, 434 faces (baked)
FEATURE [App::Link] REF_R_1206_3216Metric_dea5eb461704_ln_013  label="REF_REF_R_1206_3216Metric_6aedbf5a6e43"
  LinkPlacement = pos=(-24.1,41.1,0) rot=(0,0,1;1.5708rad)
  LinkedObject = -> Shape001
  Placement = pos=(-24.1,41.1,0) rot=(0,0,1;1.5708rad)
FEATURE [App::Link] REF_R_1206_3216Metric_dea5eb461704_ln_014  label="REF_REF_R_1206_3216Metric_874934694a7d"
  LinkPlacement = pos=(-4.6,26.9,0) rot=(0,0,1;1.5708rad)
  LinkedObject = -> Shape001
  Placement = pos=(-4.6,26.9,0) rot=(0,0,1;1.5708rad)
FEATURE [App::Link] REF_R_1206_3216Metric_dea5eb461704_ln_015  label="REF_REF_R_1206_3216Metric_748cbaacc74b"
  LinkPlacement = pos=(-4.6,45.6,0) rot=(0,0,1;1.5708rad)
  LinkedObject = -> Shape001
  Placement = pos=(-4.6,45.6,0) rot=(0,0,1;1.5708rad)
FEATURE [App::Link] REF_C_1206_3216Metric_ecc4e7f1350d_ln_016  label="REF_REF_C_1206_3216Metric_436c53fa4e84"
  LinkPlacement = pos=(-17,36,0) rot=(0,0,1;1.5708rad)
  LinkedObject = -> Shape007
  Placement = pos=(-17,36,0) rot=(0,0,1;1.5708rad)
FEATURE [App::Link] REF_SOIC_8_1EP_3_9x4_9mm_P1_27mm_EP2_29x3mm_2a411558dc4c_ln_001  label="REF_REF_SOIC-8-1EP_3.9x4.9mm_P1.27mm_EP2.29x3mm_3479d8ad36aa"
  LinkPlacement = pos=(-20.05,42.77,0) rot=(0,0,1;1.5708rad)
  LinkedObject = -> Shape012
  Placement = pos=(-20.05,42.77,0) rot=(0,0,1;1.5708rad)
FEATURE [App::Link] REF_L_Cenker_CKCS4030_d8273a953477_ln_  label="REF_REF_L_Cenker_CKCS4030_3209fc811b72"
  LinkPlacement = pos=(-29,43.4,0) rot=(0,0,1;1.5708rad)
  LinkedObject = -> Shape010
  Placement = pos=(-29,43.4,0) rot=(0,0,1;1.5708rad)
FEATURE [App::Link] REF_C_1206_3216Metric_ecc4e7f1350d_ln_017  label="REF_REF_C_1206_3216Metric_a79974573d3d"
  LinkPlacement = pos=(-30.9,48.4,0) rot=(0,0,1;3.14159rad)
  LinkedObject = -> Shape007
  Placement = pos=(-30.9,48.4,0) rot=(0,0,1;3.14159rad)
FEATURE [App::Part] Top_2375
  Group = -> [Shape,Shape001,Shape002,Shape003,Shape004,Shape005,Shape006,REF_R_Array_Convex_4x0603_e66b4cefd16a_ln_,REF_L_1206_3216Metric_923911bd139e_ln_,Shape007,REF_C_1206_3216Metric_ecc4e7f1350d_ln_,Shape008,Shape009,CQ_assembly,REF_PinHeader_1x02_P254mm_Vertical_c2c35adffc7d_ln_,REF_R_1206_3216Metric_dea5eb461704_ln_,REF_C_1206_3216Metric_ecc4e7f1350d_ln_001,REF_C_1206_3216Metric_ecc4e7f1350d_ln_002,+46 more]
  Origin = -> Origin003
FEATURE [App::Part] Step_Models_2375
  Group = -> [Top_2375]
  Origin = -> Origin002
FEATURE [App::Part] Board_2375  label="dac"
  Group = -> [Local_CS_2375,Board_Geoms_2375,Step_Models_2375]
  Origin = -> Origin001
---- part fpga_ext_board.FCStd = doc fcstd_b4e8b1fa31cf ----
FCSTD DOCUMENT  (FreeCAD 1.0R39109 (Git))
Label: fpga_ext_board
License: All rights reserved
LicenseURL: https://en.wikipedia.org/wiki/All_rights_reserved
objects: Part::Feature×4, App::Part×4, App::Link×3, PartDesign::CoordinateSystem×1, Sketcher::SketchObject×1
note: 7 computed .brp shape members not serialized (recipe doc carries the construction recipe); baked Part::Feature solids carry a one-line shape summary decoded from their .brp

FEATURE [PartDesign::CoordinateSystem] Local_CS_e45
  AttacherType = Attacher::AttachEngine3D
  MapMode = 2
FEATURE [Part::Feature] Pcb_e45
  shape: bbox 100 x 100 x 1.6 mm, 264 faces (baked)
FEATURE [Sketcher::SketchObject] PCB_Sketch_e45
  ArcFitTolerance = 1e-06
  FullyConstrained = false
  MakeInternals = false
  sketch-geometry (4):
    g0: LineSegment StartX=56.7 StartY=-51 StartZ=0 EndX=156.7 EndY=-51 EndZ=0
    g1: LineSegment StartX=156.7 StartY=-51 StartZ=0 EndX=156.7 EndY=-151 EndZ=0
    g2: LineSegment StartX=156.7 StartY=-151 StartZ=0 EndX=56.7 EndY=-151 EndZ=0
    g3: LineSegment StartX=56.7 StartY=-151 StartZ=0 EndX=56.7 EndY=-51 EndZ=0
  constraints (4):
    c: Coincident(g2,g3)
    c: Coincident(g0,g3)
    c: Coincident(g1,g2)
    c: Coincident(g0,g1)
FEATURE [App::Part] Board_Geoms_e45
  Group = -> [Pcb_e45,PCB_Sketch_e45]
  Origin = -> Origin
FEATURE [Part::Feature] Shape  label="J3_PinSocket_2x25_P2.54mm_Vertical_5b0326eaf643"
  Placement = pos=(80.9,-70.5,0) rot=(0,0,1;1.5708rad)
  shape: bbox 63.5 x 5.08 x 11.6 mm, 1310 faces (baked)
FEATURE [App::Link] J3_PinSocket_2x25_P2_54mm_Vertical_5b0326eaf643_ln_  label="J1_PinSocket_2x25_P2.54mm_Vertical_5e9946493b34"
  LinkPlacement = pos=(80.6,-131.6,0) rot=(0,0,1;1.5708rad)
  LinkedObject = -> Shape
  Placement = pos=(80.6,-131.6,0) rot=(0,0,1;1.5708rad)
FEATURE [App::Link] J3_PinSocket_2x25_P2_54mm_Vertical_5b0326eaf643_ln_001  label="J4_PinSocket_2x25_P2.54mm_Vertical_c0175bcf8e3d"
  LinkPlacement = pos=(76.56,-54.5,0) rot=(0,0,1;1.5708rad)
  LinkedObject = -> Shape
  Placement = pos=(76.56,-54.5,0) rot=(0,0,1;1.5708rad)
FEATURE [Part::Feature] Shape001  label="J6_PinHeader_1x08_P254mm_Vertical_e00167c7260b"
  Placement = pos=(116.14,-145.6,0) rot=(0,0,1;1.5708rad)
  shape: bbox 20.32 x 2.54 x 11.54 mm, 196 faces (baked)
FEATURE [Part::Feature] Shape002  label="J7_PinHeader_1x12_P254mm_Vertical_57171d797b48"
  Placement = pos=(151.3,-95.84,0) rot=(0,0,1;0rad)
  shape: bbox 2.54 x 30.48 x 11.54 mm, 292 faces (baked)
FEATURE [App::Link] J3_PinSocket_2x25_P2_54mm_Vertical_5b0326eaf643_ln_002  label="J2_PinSocket_2x25_P2.54mm_Vertical_ab23b89833e9"
  LinkPlacement = pos=(80.9,-121.3,0) rot=(0,0,1;1.5708rad)
  LinkedObject = -> Shape
  Placement = pos=(80.9,-121.3,0) rot=(0,0,1;1.5708rad)
FEATURE [App::Part] Top_e45
  Group = -> [Shape,J3_PinSocket_2x25_P2_54mm_Vertical_5b0326eaf643_ln_,J3_PinSocket_2x25_P2_54mm_Vertical_5b0326eaf643_ln_001,Shape001,Shape002,J3_PinSocket_2x25_P2_54mm_Vertical_5b0326eaf643_ln_002]
  Origin = -> Origin003
FEATURE [App::Part] Step_Models_e45
  Group = -> [Top_e45]
  Origin = -> Origin002
FEATURE [App::Part] Board_e45  label="fpga_ext_board"
  Group = -> [Local_CS_e45,Board_Geoms_e45,Step_Models_e45]
  Origin = -> Origin001
---- part frontpanel.FCStd = doc fcstd_fe6cb5f9a38a ----
FCSTD DOCUMENT  (FreeCAD 1.0R39109 (Git))
Label: frontpanel
License: All rights reserved
LicenseURL: https://en.wikipedia.org/wiki/All_rights_reserved
objects: PartDesign::Pad×5, Sketcher::SketchObject×2, PartDesign::Pocket×2, PartDesign::Hole×1, PartDesign::Fillet×1, PartDesign::Body×1
note: 32 computed .brp shape members not serialized (recipe doc carries the construction recipe); baked Part::Feature solids carry a one-line shape summary decoded from their .brp

FEATURE [Sketcher::SketchObject] Sketch
  ArcFitTolerance = 1e-06
  AttachmentSupport = -> [XY_Plane]
  FullyConstrained = false
  MakeInternals = false
  MapMode = 5
  sketch-geometry (91):
    g0: LineSegment StartX=-108.5 StartY=40.5 StartZ=0 EndX=-108.5 EndY=-40.5 EndZ=0
    g1: LineSegment StartX=-108.5 StartY=-40.5 StartZ=0 EndX=108.5 EndY=-40.5 EndZ=0
    g2: LineSegment StartX=108.5 StartY=-40.5 StartZ=0 EndX=108.5 EndY=40.5 EndZ=0
    g3: LineSegment StartX=108.5 StartY=40.5 StartZ=0 EndX=-108.5 EndY=40.5 EndZ=0
    g4: LineSegment [constr] StartX=-96.5 StartY=29.59 StartZ=0 EndX=-96.5 EndY=-29.59 EndZ=0
    g5: LineSegment [constr] StartX=-96.5 StartY=-29.59 StartZ=0 EndX=15.01 EndY=-29.59 EndZ=0
    g6: LineSegment [constr] StartX=15.01 StartY=-29.59 StartZ=0 EndX=15.01 EndY=29.59 EndZ=0
    g7: LineSegment [constr] StartX=15.01 StartY=29.59 StartZ=0 EndX=-96.5 EndY=29.59 EndZ=0
    g8: Circle CenterX=-93.5 CenterY=26.59 CenterZ=0 NormalX=0 NormalY=0 NormalZ=1 AngleXU=0 Radius=3
    g9: Circle CenterX=-93.5 CenterY=-26.59 CenterZ=0 NormalX=0 NormalY=0 NormalZ=1 AngleXU=0 Radius=3
    g10: Circle CenterX=12.01 CenterY=26.59 CenterZ=0 NormalX=0 NormalY=0 NormalZ=1 AngleXU=0 Radius=3
    g11: Circle CenterX=12.01 CenterY=-26.59 CenterZ=0 NormalX=0 NormalY=0 NormalZ=1 AngleXU=0 Radius=3
    g12: LineSegment StartX=-88.5 StartY=27.59 StartZ=0 EndX=-88.5 EndY=-27.59 EndZ=0
    g13: LineSegment StartX=-88.5 StartY=-27.59 StartZ=0 EndX=1.01 EndY=-27.59 EndZ=0
    g14: LineSegment StartX=1.01 StartY=-27.59 StartZ=0 EndX=1.01 EndY=27.59 EndZ=0
    g15: LineSegment StartX=1.01 StartY=27.59 StartZ=0 EndX=-88.5 EndY=27.59 EndZ=0
    g16: LineSegment [constr] StartX=-98.5 StartY=35.5 StartZ=0 EndX=-98.5 EndY=-35.5 EndZ=0
    g17: LineSegment [constr] StartX=-98.5 StartY=-35.5 StartZ=0 EndX=98.5 EndY=-35.5 EndZ=0
    g18: LineSegment [constr] StartX=98.5 StartY=-35.5 StartZ=0 EndX=98.5 EndY=35.5 EndZ=0
    g19: LineSegment [constr] StartX=98.5 StartY=35.5 StartZ=0 EndX=-98.5 EndY=35.5 EndZ=0
    g20: ArcOfCircle CenterX=88 CenterY=25 CenterZ=0 NormalX=0 NormalY=0 NormalZ=1 AngleXU=0 Radius=6.35 StartAngle=3.73904 EndAngle=8.82733
    g21: Circle [constr] CenterX=88 CenterY=25 CenterZ=0 NormalX=0 NormalY=0 NormalZ=1 AngleXU=0 Radius=10.5
    g22: ArcOfCircle CenterX=88 CenterY=0 CenterZ=0 NormalX=0 NormalY=0 NormalZ=1 AngleXU=0 Radius=6.35 StartAngle=3.73904 EndAngle=8.82733
    g23: Circle [constr] CenterX=88 CenterY=0 CenterZ=0 NormalX=0 NormalY=0 NormalZ=1 AngleXU=0 Radius=10.5
    g24: Circle [constr] CenterX=88 CenterY=-25 CenterZ=0 NormalX=0 NormalY=0 NormalZ=1 AngleXU=0 Radius=10.5
    g25: ArcOfCircle CenterX=88 CenterY=-25 CenterZ=0 NormalX=0 NormalY=0 NormalZ=1 AngleXU=0 Radius=6.35 StartAngle=3.73904 EndAngle=8.82733
    g26: LineSegment StartX=82.75 StartY=28.5721 StartZ=0 EndX=82.75 EndY=21.4279 EndZ=0
    g27: LineSegment [constr] StartX=94.35 StartY=28.3208 StartZ=0 EndX=94.35 EndY=23.3208 EndZ=0
    g28: LineSegment StartX=82.75 StartY=3.57211 StartZ=0 EndX=82.75 EndY=-3.57211 EndZ=0
    g29: LineSegment StartX=82.75 StartY=-21.4279 StartZ=0 EndX=82.75 EndY=-28.5721 EndZ=0
    g30: LineSegment StartX=18.01 StartY=-30.59 StartZ=0 EndX=18.01 EndY=30.59 EndZ=0
    g31: ArcOfCircle CenterX=16.01 CenterY=30.59 CenterZ=0 NormalX=0 NormalY=0 NormalZ=-1 AngleXU=0 Radius=2 StartAngle=1.5708 EndAngle=3.14159
    g32: LineSegment StartX=16.01 StartY=32.59 StartZ=0 EndX=-97.5 EndY=32.59 EndZ=0
    g33: ArcOfCircle CenterX=-97.5 CenterY=30.59 CenterZ=0 NormalX=0 NormalY=0 NormalZ=-1 AngleXU=-1.5708 Radius=2 StartAngle=1.5708 EndAngle=3.14159
    g34: LineSegment StartX=-99.5 StartY=30.59 StartZ=0 EndX=-99.5 EndY=-30.59 EndZ=0
    g35: ArcOfCircle CenterX=-97.5 CenterY=-30.59 CenterZ=0 NormalX=0 NormalY=0 NormalZ=-1 AngleXU=-3.14159 Radius=2 StartAngle=1.5708 EndAngle=3.14159
    g36: LineSegment StartX=-97.5 StartY=-32.59 StartZ=0 EndX=16.01 EndY=-32.59 EndZ=0
    g37: ArcOfCircle CenterX=16.01 CenterY=-30.59 CenterZ=0 NormalX=0 NormalY=0 NormalZ=-1 AngleXU=1.5708 Radius=2 StartAngle=1.5708 EndAngle=3.14159
    g38: LineSegment StartX=15.11 StartY=-29.59 StartZ=0 EndX=15.11 EndY=29.59 EndZ=0
    g39: ArcOfCircle CenterX=15.01 CenterY=29.59 CenterZ=0 NormalX=0 NormalY=0 NormalZ=-1 AngleXU=0 Radius=0.1 StartAngle=1.5708 EndAngle=3.14159
    g40: LineSegment StartX=15.01 StartY=29.69 StartZ=0 EndX=-96.5 EndY=29.69 EndZ=0
    g41: ArcOfCircle CenterX=-96.5 CenterY=29.59 CenterZ=0 NormalX=0 NormalY=0 NormalZ=-1 AngleXU=-1.5708 Radius=0.1 StartAngle=1.5708 EndAngle=3.14159
    g42: LineSegment StartX=-96.6 StartY=29.59 StartZ=0 EndX=-96.6 EndY=-29.59 EndZ=0
    g43: ArcOfCircle CenterX=-96.5 CenterY=-29.59 CenterZ=0 NormalX=0 NormalY=0 NormalZ=-1 AngleXU=-3.14159 Radius=0.1 StartAngle=1.5708 EndAngle=3.14159
    g44: LineSegment StartX=-96.5 StartY=-29.69 StartZ=0 EndX=15.01 EndY=-29.69 EndZ=0
    g45: ArcOfCircle CenterX=15.01 CenterY=-29.59 CenterZ=0 NormalX=0 NormalY=0 NormalZ=-1 AngleXU=1.5708 Radius=0.1 StartAngle=1.5708 EndAngle=3.14159
    g46: LineSegment StartX=34.84 StartY=34.5 StartZ=0 EndX=34.84 EndY=-34.5 EndZ=0
    g47: LineSegment StartX=35.84 StartY=-35.5 StartZ=0 EndX=36.84 EndY=-35.5 EndZ=0
    g48: LineSegment StartX=37.84 StartY=-34.5 StartZ=0 EndX=37.84 EndY=34.5 EndZ=0
    g49: LineSegment StartX=36.84 StartY=35.5 StartZ=0 EndX=35.84 EndY=35.5 EndZ=0
    g50: ArcOfCircle CenterX=35.84 CenterY=34.5 CenterZ=0 NormalX=0 NormalY=0 NormalZ=1 AngleXU=0 Radius=1 StartAngle=1.5708 EndAngle=3.14159
    g51: ArcOfCircle CenterX=35.84 CenterY=-34.5 CenterZ=0 NormalX=0 NormalY=0 NormalZ=1 AngleXU=0 Radius=1 StartAngle=3.14159 EndAngle=4.71239
    g52: ArcOfCircle CenterX=36.84 CenterY=-34.5 CenterZ=0 NormalX=0 NormalY=0 NormalZ=1 AngleXU=0 Radius=1 StartAngle=4.71239 EndAngle=6.28319
    g53: ArcOfCircle CenterX=36.84 CenterY=34.5 CenterZ=0 NormalX=0 NormalY=0 NormalZ=1 AngleXU=0 Radius=1 StartAngle=5e-16 EndAngle=1.5708
    g54: GeomPoint [constr] X=34.84 Y=35.5 Z=0
    g55: GeomPoint [constr] X=37.84 Y=-35.5 Z=0
    g56: LineSegment StartX=54.67 StartY=34.5 StartZ=0 EndX=54.67 EndY=-34.5 EndZ=0
    g57: LineSegment StartX=55.67 StartY=-35.5 StartZ=0 EndX=56.67 EndY=-35.5 EndZ=0
    g58: LineSegment StartX=57.67 StartY=-34.5 StartZ=0 EndX=57.67 EndY=34.5 EndZ=0
    g59: LineSegment StartX=56.67 StartY=35.5 StartZ=0 EndX=55.67 EndY=35.5 EndZ=0
    g60: ArcOfCircle CenterX=55.67 CenterY=34.5 CenterZ=0 NormalX=0 NormalY=0 NormalZ=1 AngleXU=0 Radius=1 StartAngle=1.5708 EndAngle=3.14159
    g61: ArcOfCircle CenterX=55.67 CenterY=-34.5 CenterZ=0 NormalX=0 NormalY=0 NormalZ=1 AngleXU=0 Radius=1 StartAngle=3.14159 EndAngle=4.71239
    g62: ArcOfCircle CenterX=56.67 CenterY=-34.5 CenterZ=0 NormalX=0 NormalY=0 NormalZ=1 AngleXU=0 Radius=1 StartAngle=4.71239 EndAngle=6.28319
    g63: ArcOfCircle CenterX=56.67 CenterY=34.5 CenterZ=0 NormalX=0 NormalY=0 NormalZ=1 AngleXU=0 Radius=1 StartAngle=2.9e-15 EndAngle=1.5708
    g64: GeomPoint [constr] X=54.67 Y=35.5 Z=0
    g65: GeomPoint [constr] X=57.67 Y=-35.5 Z=0
    g66: LineSegment StartX=74.5 StartY=34.5 StartZ=0 EndX=74.5 EndY=-34.5 EndZ=0
    g67: LineSegment StartX=75.5 StartY=-35.5 StartZ=0 EndX=76.5 EndY=-35.5 EndZ=0
    g68: LineSegment StartX=77.5 StartY=-34.5 StartZ=0 EndX=77.5 EndY=34.5 EndZ=0
    g69: LineSegment StartX=76.5 StartY=35.5 StartZ=0 EndX=75.5 EndY=35.5 EndZ=0
    g70: ArcOfCircle CenterX=75.5 CenterY=34.5 CenterZ=0 NormalX=0 NormalY=0 NormalZ=1 AngleXU=0 Radius=1 StartAngle=1.5708 EndAngle=3.14159
    g71: ArcOfCircle CenterX=75.5 CenterY=-34.5 CenterZ=0 NormalX=0 NormalY=0 NormalZ=1 AngleXU=0 Radius=1 StartAngle=3.14159 EndAngle=4.71239
    g72: ArcOfCircle CenterX=76.5 CenterY=-34.5 CenterZ=0 NormalX=0 NormalY=0 NormalZ=1 AngleXU=0 Radius=1 StartAngle=4.71239 EndAngle=6.28319
    g73: ArcOfCircle CenterX=76.5 CenterY=34.5 CenterZ=0 NormalX=0 NormalY=0 NormalZ=1 AngleXU=0 Radius=1 StartAngle=-9e-16 EndAngle=1.5708
    g74: GeomPoint [constr] X=74.5 Y=35.5 Z=0
    g75: GeomPoint [constr] X=77.5 Y=-35.5 Z=0
    g76: LineSegment [constr] StartX=18.01 StartY=29.2155 StartZ=0 EndX=34.84 EndY=29.2155 EndZ=0
    g77: LineSegment [constr] StartX=37.84 StartY=29.2458 StartZ=0 EndX=54.67 EndY=29.2458 EndZ=0
    g78: LineSegment [constr] StartX=57.67 StartY=29.2458 StartZ=0 EndX=74.5 EndY=29.2458 EndZ=0
    g79: LineSegment StartX=-100.5 StartY=35.5 StartZ=0 EndX=-100.5 EndY=-35.5 EndZ=0
    g80: LineSegment StartX=-100.5 StartY=-35.5 StartZ=0 EndX=98.5 EndY=-35.5 EndZ=0
    g81: LineSegment StartX=98.5 StartY=-35.5 StartZ=0 EndX=98.5 EndY=35.5 EndZ=0
    g82: LineSegment StartX=98.5 StartY=35.5 StartZ=0 EndX=-100.5 EndY=35.5 EndZ=0
    g83: LineSegment StartX=8.5 StartY=40.5 StartZ=0 EndX=8.5 EndY=-40.5 EndZ=0
    g84: LineSegment StartX=8.5 StartY=-40.5 StartZ=0 EndX=77.5 EndY=-40.5 EndZ=0
    g85: LineSegment StartX=77.5 StartY=-40.5 StartZ=0 EndX=77.5 EndY=40.5 EndZ=0
    g86: LineSegment StartX=77.5 StartY=40.5 StartZ=0 EndX=8.5 EndY=40.5 EndZ=0
    g87: LineSegment StartX=-98.1 StartY=2 StartZ=0 EndX=-98.1 EndY=-2 EndZ=0
    g88: LineSegment StartX=-98.1 StartY=-2 StartZ=0 EndX=-96.4 EndY=-2 EndZ=0
    g89: LineSegment StartX=-96.4 StartY=-2 StartZ=0 EndX=-96.4 EndY=2 EndZ=0
    g90: LineSegment StartX=-96.4 StartY=2 StartZ=0 EndX=-98.1 EndY=2 EndZ=0
  constraints (243):
    c: Coincident(g0,g1)
    c: Coincident(g1,g2)
    c: Coincident(g2,g3)
    c: Coincident(g3,g0)
    c: Vertical(g0)
    c: Vertical(g2)
    c: Horizontal(g1)
    c: Horizontal(g3)
    c: Distance(g0,g2) = 217
    c: Distance(g1,g3) = 81
    c: Symmetric(g0,g1,g-1)
    c: Coincident(g4,g5)
    c: Coincident(g5,g6)
    c: Coincident(g6,g7)
    c: Coincident(g7,g4)
    c: Vertical(g6)
    c: Horizontal(g5)
    c: Horizontal(g7)
    c: DistanceX(g7,g7) = 111.51
    c: DistanceY(g4,g4) = 59.18
    c: Symmetric(g4,g4,g-1)
    c: DistanceX(g0,g4) = 12
    c: Distance(g8,g4) = 3
    c: Distance(g8,g7) = 3
    c: Horizontal(g10,g8)
    c: Distance(g10,g6) = 3
    c: Vertical(g8,g9)
    c: Vertical(g11,g10)
    c: Horizontal(g9,g11)
    c: Distance(g9,g5) = 3
    c: Coincident(g12,g13)
    c: Coincident(g13,g14)
    c: Coincident(g14,g15)
    c: Coincident(g15,g12)
    c: Vertical(g12)
    c: Vertical(g14)
    c: Horizontal(g13)
    c: Horizontal(g15)
    c: Distance(g12,g4) = 8
    c: Distance(g6,g14) = 14
    c: Distance(g7,g15) = 2
    c: Distance(g5,g13) = 2
    c: Coincident(g16,g17)
    c: Coincident(g17,g18)
    c: Coincident(g18,g19)
    c: Coincident(g19,g16)
    c: Vertical(g16)
    c: Vertical(g18)
    c: Horizontal(g17)
    c: Horizontal(g19)
    c: Distance(g16,g0) = 10
    c: Distance(g18,g2) = 10
    c: Distance(g1,g17) = 5
    c: Distance(g3,g19) = 5
    c: Diameter(g20) = 12.7
    c: Diameter(g21) = 21
    c: Coincident(g21,g20)
    c: Tangent(g21,g19)
    c: Tangent(g21,g18)
    c: Diameter(g22) = 12.7
    c: Diameter(g23) = 21
    c: Coincident(g23,g22)
    c: Diameter(g24) = 21
    c: Diameter(g25) = 12.7
    c: Coincident(g25,g24)
    c: Tangent(g24,g18)
    c: Tangent(g24,g17)
    c: Diameter(g9) = 6
    c: Equal(g11,g10)
    c: Equal(g10,g8)
    c: Equal(g9,g8)
    c: Vertical(g26)
    c: Vertical(g27)
    c: Tangent(g20,g27)
    c: Distance(g27,g26) = 11.6
    c: Coincident(g20,g26)
    c: Coincident(g26,g20)
    c: Coincident(g25,g29)
    c: Coincident(g25,g29)
    c: Vertical(g28,g20)
    c: Vertical(g20,g25)
    c: Vertical(g28)
    c: Vertical(g29)
    c: PointOnObject(g22,g-1)
    c: Tangent(g23,g18)
    c: Coincident(g28,g22)
    c: Coincident(g28,g22)
    c: DistanceY(g27,g27) = 5
    c: Tangent(g30,g31) = -1.5708
    c: Tangent(g30,g37) = -1.5708
    c: Tangent(g31,g32) = -1.5708
    c: Tangent(g32,g33) = -1.5708
    c: Tangent(g33,g34) = -1.5708
    c: Tangent(g34,g35) = -1.5708
    c: Tangent(g35,g36) = -1.5708
    c: Tangent(g36,g37) = -1.5708
    c: Tangent(g38,g39) = -1.5708
    c: Tangent(g38,g45) = -1.5708
    c: Tangent(g39,g40) = -1.5708
    c: Tangent(g40,g41) = -1.5708
    c: Tangent(g41,g42) = -1.5708
    c: Tangent(g42,g43) = -1.5708
    c: Tangent(g43,g44) = -1.5708
    c: Tangent(g44,g45) = -1.5708
    c: Tangent(g46,g50) = -1.5708
    c: Tangent(g46,g51) = -1.5708
    c: Tangent(g47,g51) = -1.5708
    c: Tangent(g47,g52) = -1.5708
    c: Tangent(g48,g52) = -1.5708
    c: Tangent(g48,g53) = -1.5708
    c: Tangent(g49,g53) = -1.5708
    c: Tangent(g49,g50) = -1.5708
    c: Vertical(g46)
    c: Vertical(g48)
    c: Horizontal(g47)
    c: Horizontal(g49)
    c: Equal(g50,g51)
    c: Equal(g51,g52)
    c: Equal(g52,g53)
    c: PointOnObject(g54,g46)
    c: PointOnObject(g54,g49)
    c: PointOnObject(g55,g47)
    c: PointOnObject(g55,g48)
    c: Radius(g51) = 1
    c: Tangent(g56,g60) = -1.5708
    c: Tangent(g56,g61) = -1.5708
    c: Tangent(g57,g61) = -1.5708
    c: Tangent(g57,g62) = -1.5708
    c: Tangent(g58,g62) = -1.5708
    c: Tangent(g58,g63) = -1.5708
    c: Tangent(g59,g63) = -1.5708
    c: Tangent(g59,g60) = -1.5708
    c: Vertical(g56)
    c: Vertical(g58)
    c: Horizontal(g57)
    c: Horizontal(g59)
    c: Equal(g60,g61)
    c: Equal(g61,g62)
    c: Equal(g62,g63)
    c: PointOnObject(g64,g56)
    c: PointOnObject(g64,g59)
    c: PointOnObject(g65,g57)
    c: PointOnObject(g65,g58)
    c: Distance(g56,g58) = 3
    c: Radius(g61) = 1
    c: Tangent(g66,g70) = -1.5708
    c: Tangent(g66,g71) = -1.5708
    c: Tangent(g67,g71) = -1.5708
    c: Tangent(g67,g72) = -1.5708
    c: Tangent(g68,g72) = -1.5708
    c: Tangent(g68,g73) = -1.5708
    c: Tangent(g69,g73) = -1.5708
    c: Tangent(g69,g70) = -1.5708
    c: Vertical(g66)
    c: Vertical(g68)
    c: Horizontal(g67)
    c: Horizontal(g69)
    c: Equal(g70,g71)
    c: Equal(g71,g72)
    c: Equal(g72,g73)
    c: PointOnObject(g74,g66)
    c: PointOnObject(g74,g69)
    c: PointOnObject(g75,g67)
    c: PointOnObject(g75,g68)
    c: Distance(g66,g68) = 3
    c: Radius(g71) = 1
    c: PointOnObject(g49,g19)
    c: PointOnObject(g47,g17)
    c: PointOnObject(g57,g17)
    c: PointOnObject(g67,g17)
    c: Distance(g48,g46) = 3
    c: PointOnObject(g59,g19)
    c: PointOnObject(g69,g19)
    c: Tangent(g68,g21)
    c: PointOnObject(g76,g30)
    c: PointOnObject(g76,g46)
    c: Horizontal(g76)
    c: PointOnObject(g77,g48)
    c: PointOnObject(g77,g56)
    c: Horizontal(g77)
    c: PointOnObject(g78,g58)
    c: PointOnObject(g78,g66)
    c: Horizontal(g78)
    c: Equal(g76,g77)
    c: Equal(g77,g78)
    c: Vertical(g30)
    c: Vertical(g34)
    c: Horizontal(g32)
    c: Horizontal(g36)
    c: Vertical(g42)
    c: Vertical(g38)
    c: Horizontal(g40)
    c: Distance(g38,g6) = 0.1
    c: Distance(g40,g7) = 0.1
    c: Distance(g32,g7) = 3
    c: Distance(g30,g6) = 3
    c: Distance(g42,g4) = 0.1
    c: Distance(g34,g4) = 3
    c: Distance(g44,g5) = 0.1
    c: Distance(g36,g5) = 3
    c: Equal(g35,g33)
    c: Equal(g33,g31)
    c: Equal(g31,g37)
    c: Distance(g33,g33) = 2
    c: Radius(g41) = 0.1
    c: Radius(g39) = 0.1
    c: Radius(g45) = 0.1
    c: Radius(g43) = 0.1
    c: Horizontal(g44)
    c: Coincident(g79,g80)
    c: Coincident(g80,g81)
    c: Coincident(g81,g82)
    c: Coincident(g82,g79)
    c: Vertical(g79)
    c: Vertical(g81)
    c: Horizontal(g80)
    c: Horizontal(g82)
    c: PointOnObject(g79,g19)
    c: Coincident(g80,g17)
    c: Coincident(g83,g84)
    c: Coincident(g84,g85)
    c: Coincident(g85,g86)
    c: Coincident(g86,g83)
    c: Vertical(g83)
    c: Vertical(g85)
    c: Horizontal(g84)
    c: Horizontal(g86)
    c: Distance(g83,g85) = 69
    c: PointOnObject(g83,g3)
    c: PointOnObject(g84,g1)
    c: Tangent(g23,g85)
    c: Distance(g34,g79) = 1
    c: Coincident(g87,g88)
    c: Coincident(g88,g89)
    c: Coincident(g89,g90)
    c: Coincident(g90,g87)
    c: Vertical(g89)
    c: Horizontal(g88)
    c: Horizontal(g90)
    c: Distance(g87,g89) = 1.7
    c: Distance(g88,g90) = 4
    c: Symmetric(g87,g87,g-1)
    c: Distance(g89,g42) = 0.2
FEATURE [PartDesign::Pad] Pad
  Direction = (0,0,1)
  Length = 2
  Length2 = 10
  Profile = -> Sketch [Edge12,Edge4,Edge1,Edge2,Edge3,Edge11,Edge10,Edge9,Edge17,Edge18,Edge16,Edge15,Edge13,Edge14]
  ReferenceAxis = -> Sketch [N_Axis]
  Refine = true
  Suppressed = false
  Type = 0
FEATURE [PartDesign::Pad] Pad001
  BaseFeature = -> Pad
  Direction = (0,0,1)
  Length = 3
  Length2 = 10
  Profile = -> Sketch [Edge8,Edge7,Edge5,Edge6]
  ReferenceAxis = -> Sketch [N_Axis]
  Refine = true
  Reversed = true
  Suppressed = false
  Type = 0
FEATURE [PartDesign::Hole] Hole
  BaseFeature = -> Pad001
  CustomThreadClearance = 0
  Depth = 25
  DepthType = 0
  Diameter = 2.52
  DrillForDepth = false
  DrillPoint = 1
  DrillPointAngle = 118
  HoleCutCountersinkAngle = 90
  HoleCutCustomValues = false
  HoleCutDepth = 0
  HoleCutDiameter = 6.1
  HoleCutType = 0
  ModelThread = true
  Profile = -> Sketch [Edge5,Edge6,Edge8,Edge7]
  Refine = true
  Suppressed = false
  Tapered = false
  TaperedAngle = 90
  ThreadClass = 0
  ThreadDepth = 4
  ThreadDepthType = 1
  ThreadDirection = 0
  ThreadFit = 0
  ThreadSize = 9
  ThreadType = 1
  Threaded = true
  UseCustomThreadClearance = false
FEATURE [PartDesign::Fillet] Fillet
  Base = -> Hole [Edge28,Edge27,Edge29,Edge30]
  BaseFeature = -> Hole
  Radius = 1.6
  Refine = true
  SupportTransform = false
  Suppressed = false
  UseAllEdges = false
FEATURE [PartDesign::Pad] Pad002
  BaseFeature = -> Fillet
  Direction = (0,0,1)
  Length = 10
  Length2 = 10
  Profile = -> Sketch [Edge35,Edge39,Edge43,Edge47,Edge51,Edge55,Edge54,Edge53,Edge52,Edge46,Edge45,Edge44,Edge38,Edge37,Edge36,Edge42,Edge41,Edge40,Edge50,Edge49,Edge48,Edge58,Edge57,Edge56]
  ReferenceAxis = -> Sketch [N_Axis]
  Refine = true
  Reversed = true
  Suppressed = false
  Type = 0
FEATURE [PartDesign::Pad] Pad003
  BaseFeature = -> Pad002
  Direction = (0,0,1)
  Length = 10
  Length2 = 10
  Profile = -> Sketch [Edge31,Edge23,Edge22,Edge21,Edge30,Edge29,Edge32,Edge33,Edge24,Edge25,Edge26,Edge19,Edge34,Edge27,Edge20,Edge28]
  ReferenceAxis = -> Sketch [N_Axis]
  Refine = true
  Reversed = true
  Suppressed = false
  Type = 0
FEATURE [Sketcher::SketchObject] Sketch001
  ArcFitTolerance = 1e-06
  FullyConstrained = false
  MakeInternals = false
  MapMode = 5
  Placement = pos=(0,0,2) rot=(0,0,1;0rad)
  sketch-geometry (4):
    g0: LineSegment StartX=8.54706 StartY=49.6001 StartZ=0 EndX=8.54706 EndY=-45.1489 EndZ=0
    g1: LineSegment StartX=8.54706 StartY=-45.1489 StartZ=0 EndX=77.5471 EndY=-45.1489 EndZ=0
    g2: LineSegment StartX=77.5471 StartY=-45.1489 StartZ=0 EndX=77.5471 EndY=49.6001 EndZ=0
    g3: LineSegment StartX=77.5471 StartY=49.6001 StartZ=0 EndX=8.54706 EndY=49.6001 EndZ=0
  constraints (9):
    c: Coincident(g0,g1)
    c: Coincident(g1,g2)
    c: Coincident(g2,g3)
    c: Coincident(g3,g0)
    c: Vertical(g0)
    c: Vertical(g2)
    c: Horizontal(g1)
    c: Horizontal(g3)
    c: Distance(g0,g2) = 69
FEATURE [PartDesign::Pocket] Pocket
  BaseFeature = -> Pad003
  Direction = (0,0,-1)
  Length = 0.5
  Length2 = 5
  Profile = -> Sketch001
  ReferenceAxis = -> Sketch001 [N_Axis]
  Refine = true
  Suppressed = false
  Type = 0
FEATURE [PartDesign::Pad] Pad004
  BaseFeature = -> Pocket
  Direction = (0,0,1)
  Length = 3
  Length2 = 10
  Profile = -> Sketch [Edge59,Edge62,Edge21,Edge22,Edge23,Edge60,Edge25,Edge24,Edge26,Edge19,Edge20,Edge61,Edge17,Edge15,Edge13,Edge14,Edge16,Edge18]
  ReferenceAxis = -> Sketch [N_Axis]
  Refine = true
  Reversed = true
  Suppressed = false
  Type = 0
FEATURE [PartDesign::Pocket] Pocket001
  BaseFeature = -> Pad004
  Direction = (0,0,-1)
  Length = 10
  Length2 = -4
  Profile = -> Sketch [Edge70,Edge67,Edge68,Edge69]
  ReferenceAxis = -> Sketch [N_Axis]
  Refine = true
  Suppressed = false
  Type = 4
  UpToShape = -> [Pad004]
FEATURE [PartDesign::Body] Body  label="front panel"
  AllowCompound = false
  Group = -> [Sketch,Pad,Pad001,Hole,Fillet,Pad002,Pad003,Sketch001,Pocket,Pad004,Pocket001]
  Origin = -> Origin
  Tip = -> Pocket001
